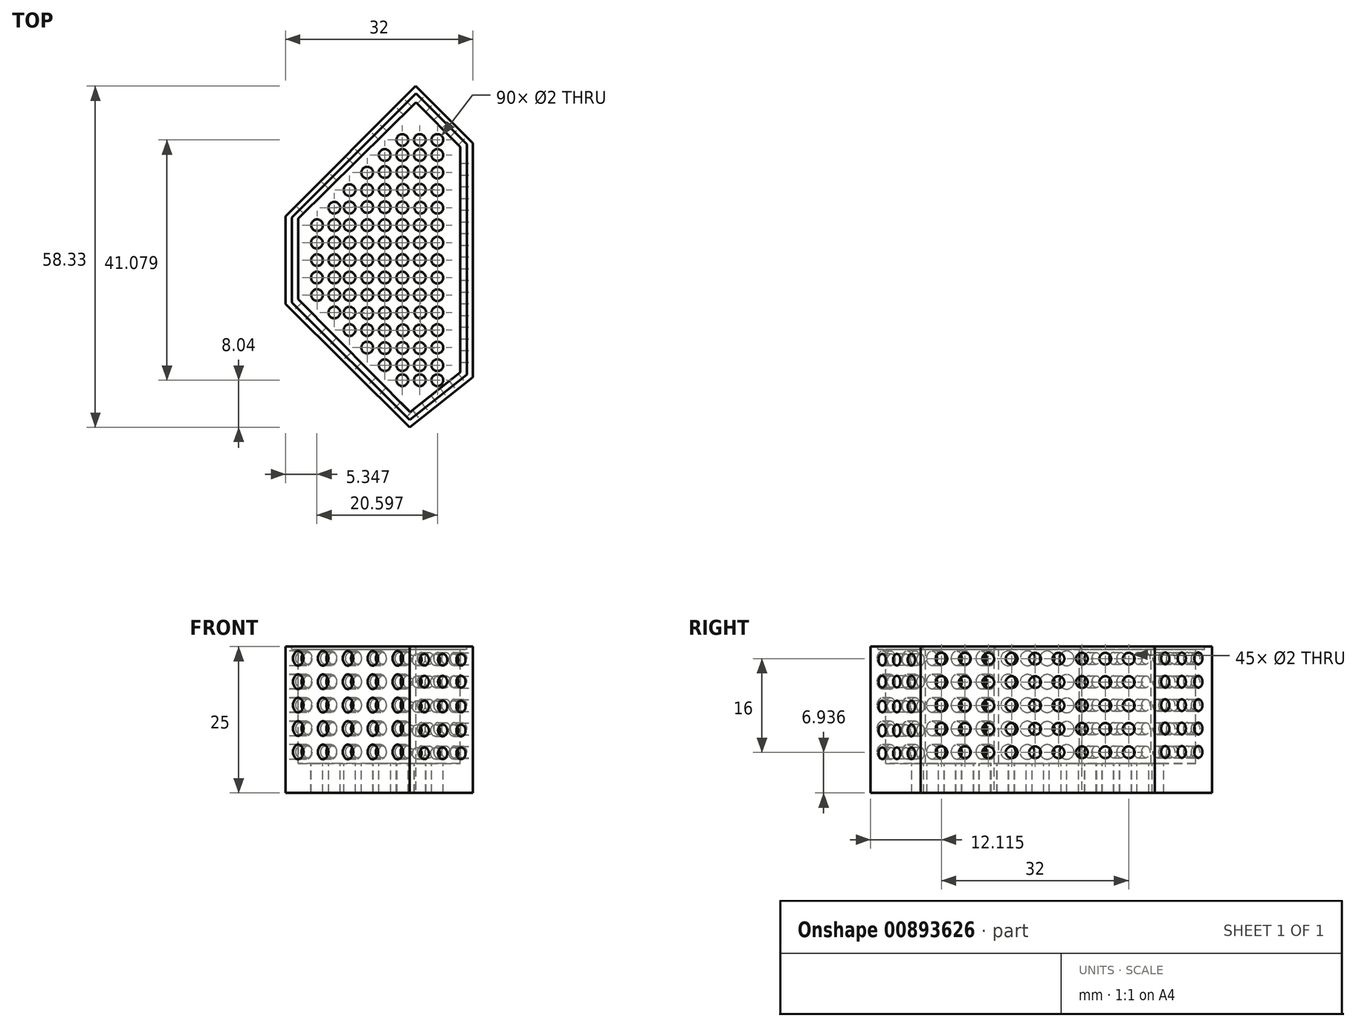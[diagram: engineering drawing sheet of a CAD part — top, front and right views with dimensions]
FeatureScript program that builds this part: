
annotation { "Feature Type Name" : "Feature", "Feature Type Description" : "" }
export const myFeature = defineFeature(function(context is Context, id is Id, definition is map)
    precondition{}
    {
        {
            var Q0;
            Q0=qCreatedBy(makeId("Top.planeOp"),FACE);
            var sketch = newSketch(context, id + "F0", { "sketchPlane" : qUnion([Q0])});
            skLineSegment(sketch, "E0", {"start": v(10.6, 0) * mm, "end": v(10.6, 7.5) * mm});
            skLineSegment(sketch, "E1", {"start": v(42.6, 0) * mm, "end": v(42.6, 20) * mm});
            skLineSegment(sketch, "E2", {"start": v(10.6, 7.5) * mm, "end": v(32.85, 29.75) * mm});
            skLineSegment(sketch, "E3", {"start": v(42.6, 20) * mm, "end": v(32.85, 29.75) * mm});
            skLineSegment(sketch, "E4", {"start": v(10.6, 0) * mm, "end": v(10.6, -7.5) * mm});
            skLineSegment(sketch, "E5", {"start": v(42.6, 0) * mm, "end": v(42.6, -20) * mm});
            skLineSegment(sketch, "E6", {"start": v(31.8, -28.58) * mm, "end": v(10.6, -7.5) * mm});
            skLineSegment(sketch, "E7", {"start": v(42.6, -20) * mm, "end": v(31.8, -28.58) * mm});
            skSolve(sketch);
        }
        {
            var Q0;
            Q0=makeQuery(id+"F0.imprint","IMPRINT",FACE,{"disambiguationData":[TD([[makeQuery(id+"F0.imprint","IMPRINT",EDGE,{"derivedFrom":sQuery(id+"F0.wireOp",EDGE,"E0")}),-1.0]])]});
            extrude(context, id + "F1", {"entities" : qUnion([Q0]), "depth" : 25 * mm, "offsetDistance" : 25 * mm});
        }
        {
            var Q0;
            Q0=makeQuery(id+"F1.opExtrude","CAP_FACE",FACE,{"disambiguationData":[OSD([sQuery(id+"F0.wireOp",EDGE,"E0"),sQuery(id+"F0.wireOp",EDGE,"E1"),sQuery(id+"F0.wireOp",EDGE,"E2"),sQuery(id+"F0.wireOp",EDGE,"E3"),sQuery(id+"F0.wireOp",EDGE,"E4"),sQuery(id+"F0.wireOp",EDGE,"E5"),sQuery(id+"F0.wireOp",EDGE,"E6"),sQuery(id+"F0.wireOp",EDGE,"E7")])],"isStart":false});
            var sketch = newSketch(context, id + "F2", { "sketchPlane" : qUnion([Q0])});
            skLineSegment(sketch, "E8", {"start": v(11.67, 0) * mm, "end": v(11.67, 7.32) * mm});
            skLineSegment(sketch, "E9", {"start": v(11.67, 7.32) * mm, "end": v(32.88, 28.52) * mm});
            skLineSegment(sketch, "E10", {"start": v(32.88, 28.52) * mm, "end": v(41.61, 19.79) * mm});
            skLineSegment(sketch, "E11", {"start": v(41.61, 19.79) * mm, "end": v(41.61, 0) * mm});
            skLineSegment(sketch, "E12", {"start": v(41.61, 0) * mm, "end": v(41.61, -19.55) * mm});
            skLineSegment(sketch, "E13", {"start": v(41.61, -19.55) * mm, "end": v(31.8, -27.35) * mm});
            skLineSegment(sketch, "E14", {"start": v(31.8, -27.35) * mm, "end": v(11.67, -7.23) * mm});
            skLineSegment(sketch, "E15", {"start": v(11.67, -7.23) * mm, "end": v(11.67, 0) * mm});
            skSolve(sketch);
        }
        {
            var Q0;
            Q0=makeQuery(id+"F2.imprint","IMPRINT",FACE,{"disambiguationData":[TD([[makeQuery(id+"F2.imprint","IMPRINT",EDGE,{"derivedFrom":sQuery(id+"F2.wireOp",EDGE,"E8")}),-1.0]])]});
            var sketch = newSketch(context, id + "F3", { "sketchPlane" : qUnion([Q0])});
            skLineSegment(sketch, "E16", {"start": v(12.76, 0) * mm, "end": v(12.76, 7.1) * mm});
            skLineSegment(sketch, "E17", {"start": v(12.76, 7.1) * mm, "end": v(32.86, 27) * mm});
            skLineSegment(sketch, "E18", {"start": v(32.86, 27) * mm, "end": v(40.43, 19.36) * mm});
            skLineSegment(sketch, "E19", {"start": v(40.43, 19.36) * mm, "end": v(40.43, 0) * mm});
            skLineSegment(sketch, "E20", {"start": v(40.43, 0) * mm, "end": v(40.43, -19.16) * mm});
            skLineSegment(sketch, "E21", {"start": v(40.43, -19.16) * mm, "end": v(31.9, -25.96) * mm});
            skLineSegment(sketch, "E22", {"start": v(31.9, -25.96) * mm, "end": v(12.76, -6.7) * mm});
            skLineSegment(sketch, "E23", {"start": v(12.76, -6.7) * mm, "end": v(12.76, 0) * mm});
            skSolve(sketch);
        }
        {
            var Q0;
            Q0=makeQuery(id+"F3.imprint","IMPRINT",FACE,{"disambiguationData":[TD([[makeQuery(id+"F3.imprint","IMPRINT",EDGE,{"derivedFrom":sQuery(id+"F3.wireOp",EDGE,"E16")}),-1.0]])]});
            extrude(context, id + "F4", {"entities" : qUnion([Q0]), "operationType" : NewBodyOperationType.REMOVE, "oppositeDirection" : true, "depth" : 20 * mm, "offsetDistance" : 25 * mm});
        }
        {
            var Q0;
            Q0=makeQuery(id+"F1.opExtrude","SWEPT_FACE",FACE,{"disambiguationData":[OSD([sQuery(id+"F0.wireOp",EDGE,"E1"),sQuery(id+"F0.wireOp",EDGE,"E5")])]});
            var sketch = newSketch(context, id + "F5", { "sketchPlane" : qUnion([Q0])});
            skLineSegment(sketch, "E24.bottom", {"start": v(-18.47, 22.94) * mm, "end": v(-16.47, 22.94) * mm});
            skLineSegment(sketch, "E24.top", {"start": v(-18.47, 20.94) * mm, "end": v(-16.47, 20.94) * mm});
            skLineSegment(sketch, "E24.left", {"start": v(-18.47, 22.94) * mm, "end": v(-18.47, 20.94) * mm});
            skLineSegment(sketch, "E24.right", {"start": v(-16.47, 22.94) * mm, "end": v(-16.47, 20.94) * mm});
            skPoint(sketch, "E25.oppositeSnap0", {"position": v(-14.47, 22.94) * mm});
            skLineSegment(sketch, "E25.bottom", {"start": v(-12.47, 22.94) * mm, "end": v(-14.47, 22.94) * mm});
            skLineSegment(sketch, "E25.top", {"start": v(-12.47, 20.94) * mm, "end": v(-14.47, 20.94) * mm});
            skLineSegment(sketch, "E25.left", {"start": v(-12.47, 22.94) * mm, "end": v(-12.47, 20.94) * mm});
            skLineSegment(sketch, "E25.right", {"start": v(-14.47, 22.94) * mm, "end": v(-14.47, 20.94) * mm});
            skLineSegment(sketch, "E26.bottom", {"start": v(-8.47, 22.94) * mm, "end": v(-10.47, 22.94) * mm});
            skLineSegment(sketch, "E26.top", {"start": v(-8.47, 20.94) * mm, "end": v(-10.47, 20.94) * mm});
            skLineSegment(sketch, "E26.left", {"start": v(-8.47, 22.94) * mm, "end": v(-8.47, 20.94) * mm});
            skLineSegment(sketch, "E26.right", {"start": v(-10.47, 22.94) * mm, "end": v(-10.47, 20.94) * mm});
            skLineSegment(sketch, "E27.bottom", {"start": v(-4.47, 22.94) * mm, "end": v(-6.47, 22.94) * mm});
            skLineSegment(sketch, "E27.top", {"start": v(-4.47, 20.94) * mm, "end": v(-6.47, 20.94) * mm});
            skLineSegment(sketch, "E27.left", {"start": v(-4.47, 22.94) * mm, "end": v(-4.47, 20.94) * mm});
            skLineSegment(sketch, "E27.right", {"start": v(-6.47, 22.94) * mm, "end": v(-6.47, 20.94) * mm});
            skPoint(sketch, "E28.oppositeSnap0", {"position": v(-2.47, 22.94) * mm});
            skLineSegment(sketch, "E28.bottom", {"start": v(-0.47, 22.94) * mm, "end": v(-2.47, 22.94) * mm});
            skLineSegment(sketch, "E28.top", {"start": v(-0.47, 20.94) * mm, "end": v(-2.47, 20.94) * mm});
            skLineSegment(sketch, "E28.left", {"start": v(-0.47, 22.94) * mm, "end": v(-0.47, 20.94) * mm});
            skLineSegment(sketch, "E28.right", {"start": v(-2.47, 22.94) * mm, "end": v(-2.47, 20.94) * mm});
            skLineSegment(sketch, "E29.bottom", {"start": v(3.53, 22.94) * mm, "end": v(1.53, 22.94) * mm});
            skLineSegment(sketch, "E29.top", {"start": v(3.53, 20.94) * mm, "end": v(1.53, 20.94) * mm});
            skLineSegment(sketch, "E29.left", {"start": v(3.53, 22.94) * mm, "end": v(3.53, 20.94) * mm});
            skLineSegment(sketch, "E29.right", {"start": v(1.53, 22.94) * mm, "end": v(1.53, 20.94) * mm});
            skLineSegment(sketch, "E30.bottom", {"start": v(7.53, 22.94) * mm, "end": v(5.53, 22.94) * mm});
            skLineSegment(sketch, "E30.top", {"start": v(7.53, 20.94) * mm, "end": v(5.53, 20.94) * mm});
            skLineSegment(sketch, "E30.left", {"start": v(7.53, 22.94) * mm, "end": v(7.53, 20.94) * mm});
            skLineSegment(sketch, "E30.right", {"start": v(5.53, 22.94) * mm, "end": v(5.53, 20.94) * mm});
            skLineSegment(sketch, "E31.bottom", {"start": v(11.53, 22.94) * mm, "end": v(9.53, 22.94) * mm});
            skLineSegment(sketch, "E31.top", {"start": v(11.53, 20.94) * mm, "end": v(9.53, 20.94) * mm});
            skLineSegment(sketch, "E31.left", {"start": v(11.53, 22.94) * mm, "end": v(11.53, 20.94) * mm});
            skLineSegment(sketch, "E31.right", {"start": v(9.53, 22.94) * mm, "end": v(9.53, 20.94) * mm});
            skLineSegment(sketch, "E32.bottom", {"start": v(15.53, 22.94) * mm, "end": v(13.53, 22.94) * mm});
            skLineSegment(sketch, "E32.top", {"start": v(15.53, 20.94) * mm, "end": v(13.53, 20.94) * mm});
            skLineSegment(sketch, "E32.left", {"start": v(15.53, 22.94) * mm, "end": v(15.53, 20.94) * mm});
            skLineSegment(sketch, "E32.right", {"start": v(13.53, 22.94) * mm, "end": v(13.53, 20.94) * mm});
            skLineSegment(sketch, "E33.bottom", {"start": v(-18.47, 16.94) * mm, "end": v(-16.47, 16.94) * mm});
            skLineSegment(sketch, "E33.top", {"start": v(-18.47, 18.94) * mm, "end": v(-16.47, 18.94) * mm});
            skLineSegment(sketch, "E33.left", {"start": v(-18.47, 16.94) * mm, "end": v(-18.47, 18.94) * mm});
            skLineSegment(sketch, "E33.right", {"start": v(-16.47, 16.94) * mm, "end": v(-16.47, 18.94) * mm});
            skLineSegment(sketch, "E34.bottom", {"start": v(-12.47, 16.94) * mm, "end": v(-14.47, 16.94) * mm});
            skLineSegment(sketch, "E34.top", {"start": v(-12.47, 18.94) * mm, "end": v(-14.47, 18.94) * mm});
            skLineSegment(sketch, "E34.left", {"start": v(-12.47, 16.94) * mm, "end": v(-12.47, 18.94) * mm});
            skLineSegment(sketch, "E34.right", {"start": v(-14.47, 16.94) * mm, "end": v(-14.47, 18.94) * mm});
            skLineSegment(sketch, "E35.bottom", {"start": v(-8.47, 16.94) * mm, "end": v(-10.47, 16.94) * mm});
            skLineSegment(sketch, "E35.top", {"start": v(-8.47, 18.94) * mm, "end": v(-10.47, 18.94) * mm});
            skLineSegment(sketch, "E35.left", {"start": v(-8.47, 16.94) * mm, "end": v(-8.47, 18.94) * mm});
            skLineSegment(sketch, "E35.right", {"start": v(-10.47, 16.94) * mm, "end": v(-10.47, 18.94) * mm});
            skLineSegment(sketch, "E36.bottom", {"start": v(-4.47, 16.94) * mm, "end": v(-6.47, 16.94) * mm});
            skLineSegment(sketch, "E36.top", {"start": v(-4.47, 18.94) * mm, "end": v(-6.47, 18.94) * mm});
            skLineSegment(sketch, "E36.left", {"start": v(-4.47, 16.94) * mm, "end": v(-4.47, 18.94) * mm});
            skLineSegment(sketch, "E36.right", {"start": v(-6.47, 16.94) * mm, "end": v(-6.47, 18.94) * mm});
            skLineSegment(sketch, "E37.bottom", {"start": v(-0.47, 16.94) * mm, "end": v(-2.47, 16.94) * mm});
            skLineSegment(sketch, "E37.top", {"start": v(-0.47, 18.94) * mm, "end": v(-2.47, 18.94) * mm});
            skLineSegment(sketch, "E37.left", {"start": v(-0.47, 16.94) * mm, "end": v(-0.47, 18.94) * mm});
            skLineSegment(sketch, "E37.right", {"start": v(-2.47, 16.94) * mm, "end": v(-2.47, 18.94) * mm});
            skLineSegment(sketch, "E38.bottom", {"start": v(3.53, 16.94) * mm, "end": v(1.53, 16.94) * mm});
            skLineSegment(sketch, "E38.top", {"start": v(3.53, 18.94) * mm, "end": v(1.53, 18.94) * mm});
            skLineSegment(sketch, "E38.left", {"start": v(3.53, 16.94) * mm, "end": v(3.53, 18.94) * mm});
            skLineSegment(sketch, "E38.right", {"start": v(1.53, 16.94) * mm, "end": v(1.53, 18.94) * mm});
            skLineSegment(sketch, "E39.bottom", {"start": v(7.53, 16.94) * mm, "end": v(5.53, 16.94) * mm});
            skLineSegment(sketch, "E39.top", {"start": v(7.53, 18.94) * mm, "end": v(5.53, 18.94) * mm});
            skLineSegment(sketch, "E39.left", {"start": v(7.53, 16.94) * mm, "end": v(7.53, 18.94) * mm});
            skLineSegment(sketch, "E39.right", {"start": v(5.53, 16.94) * mm, "end": v(5.53, 18.94) * mm});
            skLineSegment(sketch, "E40.bottom", {"start": v(11.53, 16.94) * mm, "end": v(9.53, 16.94) * mm});
            skLineSegment(sketch, "E40.top", {"start": v(11.53, 18.94) * mm, "end": v(9.53, 18.94) * mm});
            skLineSegment(sketch, "E40.left", {"start": v(11.53, 16.94) * mm, "end": v(11.53, 18.94) * mm});
            skLineSegment(sketch, "E40.right", {"start": v(9.53, 16.94) * mm, "end": v(9.53, 18.94) * mm});
            skLineSegment(sketch, "E41.bottom", {"start": v(15.53, 16.94) * mm, "end": v(13.53, 16.94) * mm});
            skLineSegment(sketch, "E41.top", {"start": v(15.53, 18.94) * mm, "end": v(13.53, 18.94) * mm});
            skLineSegment(sketch, "E41.left", {"start": v(15.53, 16.94) * mm, "end": v(15.53, 18.94) * mm});
            skLineSegment(sketch, "E41.right", {"start": v(13.53, 16.94) * mm, "end": v(13.53, 18.94) * mm});
            skLineSegment(sketch, "E42.bottom", {"start": v(-18.47, 12.94) * mm, "end": v(-16.47, 12.94) * mm});
            skLineSegment(sketch, "E42.top", {"start": v(-18.47, 14.94) * mm, "end": v(-16.47, 14.94) * mm});
            skLineSegment(sketch, "E42.left", {"start": v(-18.47, 12.94) * mm, "end": v(-18.47, 14.94) * mm});
            skLineSegment(sketch, "E42.right", {"start": v(-16.47, 12.94) * mm, "end": v(-16.47, 14.94) * mm});
            skLineSegment(sketch, "E43.bottom", {"start": v(-12.47, 12.94) * mm, "end": v(-14.47, 12.94) * mm});
            skLineSegment(sketch, "E43.top", {"start": v(-12.47, 14.94) * mm, "end": v(-14.47, 14.94) * mm});
            skLineSegment(sketch, "E43.left", {"start": v(-12.47, 12.94) * mm, "end": v(-12.47, 14.94) * mm});
            skLineSegment(sketch, "E43.right", {"start": v(-14.47, 12.94) * mm, "end": v(-14.47, 14.94) * mm});
            skLineSegment(sketch, "E44.bottom", {"start": v(-8.47, 12.94) * mm, "end": v(-10.47, 12.94) * mm});
            skLineSegment(sketch, "E44.top", {"start": v(-8.47, 14.94) * mm, "end": v(-10.47, 14.94) * mm});
            skLineSegment(sketch, "E44.left", {"start": v(-8.47, 12.94) * mm, "end": v(-8.47, 14.94) * mm});
            skLineSegment(sketch, "E44.right", {"start": v(-10.47, 12.94) * mm, "end": v(-10.47, 14.94) * mm});
            skLineSegment(sketch, "E45.bottom", {"start": v(-4.47, 12.94) * mm, "end": v(-6.47, 12.94) * mm});
            skLineSegment(sketch, "E45.top", {"start": v(-4.47, 14.94) * mm, "end": v(-6.47, 14.94) * mm});
            skLineSegment(sketch, "E45.left", {"start": v(-4.47, 12.94) * mm, "end": v(-4.47, 14.94) * mm});
            skLineSegment(sketch, "E45.right", {"start": v(-6.47, 12.94) * mm, "end": v(-6.47, 14.94) * mm});
            skLineSegment(sketch, "E46.bottom", {"start": v(-0.47, 12.94) * mm, "end": v(-2.47, 12.94) * mm});
            skLineSegment(sketch, "E46.top", {"start": v(-0.47, 14.94) * mm, "end": v(-2.47, 14.94) * mm});
            skLineSegment(sketch, "E46.left", {"start": v(-0.47, 12.94) * mm, "end": v(-0.47, 14.94) * mm});
            skLineSegment(sketch, "E46.right", {"start": v(-2.47, 12.94) * mm, "end": v(-2.47, 14.94) * mm});
            skLineSegment(sketch, "E47.bottom", {"start": v(3.53, 12.94) * mm, "end": v(3.53, 12.94) * mm});
            skLineSegment(sketch, "E47.top", {"start": v(3.53, 13.59) * mm, "end": v(3.53, 13.59) * mm});
            skLineSegment(sketch, "E47.left", {"start": v(3.53, 12.94) * mm, "end": v(3.53, 13.59) * mm});
            skLineSegment(sketch, "E47.right", {"start": v(3.53, 12.94) * mm, "end": v(3.53, 13.59) * mm});
            skLineSegment(sketch, "E48.bottom", {"start": v(3.53, 12.94) * mm, "end": v(1.53, 12.94) * mm});
            skLineSegment(sketch, "E48.top", {"start": v(3.53, 14.94) * mm, "end": v(1.53, 14.94) * mm});
            skLineSegment(sketch, "E48.left", {"start": v(3.53, 12.94) * mm, "end": v(3.53, 14.94) * mm});
            skLineSegment(sketch, "E48.right", {"start": v(1.53, 12.94) * mm, "end": v(1.53, 14.94) * mm});
            skLineSegment(sketch, "E49.bottom", {"start": v(7.53, 12.94) * mm, "end": v(5.53, 12.94) * mm});
            skLineSegment(sketch, "E49.top", {"start": v(7.53, 14.94) * mm, "end": v(5.53, 14.94) * mm});
            skLineSegment(sketch, "E49.left", {"start": v(7.53, 12.94) * mm, "end": v(7.53, 14.94) * mm});
            skLineSegment(sketch, "E49.right", {"start": v(5.53, 12.94) * mm, "end": v(5.53, 14.94) * mm});
            skLineSegment(sketch, "E50.bottom", {"start": v(11.53, 12.94) * mm, "end": v(9.53, 12.94) * mm});
            skLineSegment(sketch, "E50.top", {"start": v(11.53, 14.94) * mm, "end": v(9.53, 14.94) * mm});
            skLineSegment(sketch, "E50.left", {"start": v(11.53, 12.94) * mm, "end": v(11.53, 14.94) * mm});
            skLineSegment(sketch, "E50.right", {"start": v(9.53, 12.94) * mm, "end": v(9.53, 14.94) * mm});
            skLineSegment(sketch, "E51.bottom", {"start": v(15.53, 12.94) * mm, "end": v(13.53, 12.94) * mm});
            skLineSegment(sketch, "E51.top", {"start": v(15.53, 14.94) * mm, "end": v(13.53, 14.94) * mm});
            skLineSegment(sketch, "E51.left", {"start": v(15.53, 12.94) * mm, "end": v(15.53, 14.94) * mm});
            skLineSegment(sketch, "E51.right", {"start": v(13.53, 12.94) * mm, "end": v(13.53, 14.94) * mm});
            skLineSegment(sketch, "E52.MirrorCS", {"start": v(-18.47, 8.94) * mm, "end": v(-16.47, 8.94) * mm});
            skLineSegment(sketch, "E53.MirrorCS", {"start": v(-18.47, 10.94) * mm, "end": v(-18.47, 8.94) * mm});
            skLineSegment(sketch, "E54.top", {"start": v(-18.47, 10.94) * mm, "end": v(-16.47, 10.94) * mm});
            skLineSegment(sketch, "E54.left", {"start": v(-18.47, 8.94) * mm, "end": v(-18.47, 10.94) * mm});
            skLineSegment(sketch, "E54.right", {"start": v(-16.47, 8.94) * mm, "end": v(-16.47, 10.94) * mm});
            skLineSegment(sketch, "E55.bottom", {"start": v(-12.47, 8.94) * mm, "end": v(-14.47, 8.94) * mm});
            skLineSegment(sketch, "E55.top", {"start": v(-12.47, 10.94) * mm, "end": v(-14.47, 10.94) * mm});
            skLineSegment(sketch, "E55.left", {"start": v(-12.47, 8.94) * mm, "end": v(-12.47, 10.94) * mm});
            skLineSegment(sketch, "E55.right", {"start": v(-14.47, 8.94) * mm, "end": v(-14.47, 10.94) * mm});
            skLineSegment(sketch, "E56.bottom", {"start": v(-8.47, 8.94) * mm, "end": v(-10.47, 8.94) * mm});
            skLineSegment(sketch, "E56.top", {"start": v(-8.47, 10.94) * mm, "end": v(-10.47, 10.94) * mm});
            skLineSegment(sketch, "E56.left", {"start": v(-8.47, 8.94) * mm, "end": v(-8.47, 10.94) * mm});
            skLineSegment(sketch, "E56.right", {"start": v(-10.47, 8.94) * mm, "end": v(-10.47, 10.94) * mm});
            skLineSegment(sketch, "E57.bottom", {"start": v(-4.47, 8.94) * mm, "end": v(-6.47, 8.94) * mm});
            skLineSegment(sketch, "E57.top", {"start": v(-4.47, 10.94) * mm, "end": v(-6.47, 10.94) * mm});
            skLineSegment(sketch, "E57.left", {"start": v(-4.47, 8.94) * mm, "end": v(-4.47, 10.94) * mm});
            skLineSegment(sketch, "E57.right", {"start": v(-6.47, 8.94) * mm, "end": v(-6.47, 10.94) * mm});
            skLineSegment(sketch, "E58.bottom", {"start": v(-0.47, 8.94) * mm, "end": v(-2.47, 8.94) * mm});
            skLineSegment(sketch, "E58.top", {"start": v(-0.47, 10.94) * mm, "end": v(-2.47, 10.94) * mm});
            skLineSegment(sketch, "E58.left", {"start": v(-0.47, 8.94) * mm, "end": v(-0.47, 10.94) * mm});
            skLineSegment(sketch, "E58.right", {"start": v(-2.47, 8.94) * mm, "end": v(-2.47, 10.94) * mm});
            skLineSegment(sketch, "E59.bottom", {"start": v(3.53, 8.94) * mm, "end": v(1.53, 8.94) * mm});
            skLineSegment(sketch, "E59.top", {"start": v(3.53, 10.94) * mm, "end": v(1.53, 10.94) * mm});
            skLineSegment(sketch, "E59.left", {"start": v(3.53, 8.94) * mm, "end": v(3.53, 10.94) * mm});
            skLineSegment(sketch, "E59.right", {"start": v(1.53, 8.94) * mm, "end": v(1.53, 10.94) * mm});
            skLineSegment(sketch, "E60.bottom", {"start": v(7.53, 8.94) * mm, "end": v(5.53, 8.94) * mm});
            skLineSegment(sketch, "E60.top", {"start": v(7.53, 10.94) * mm, "end": v(5.53, 10.94) * mm});
            skLineSegment(sketch, "E60.left", {"start": v(7.53, 8.94) * mm, "end": v(7.53, 10.94) * mm});
            skLineSegment(sketch, "E60.right", {"start": v(5.53, 8.94) * mm, "end": v(5.53, 10.94) * mm});
            skLineSegment(sketch, "E61.bottom", {"start": v(11.53, 8.94) * mm, "end": v(9.53, 8.94) * mm});
            skLineSegment(sketch, "E61.top", {"start": v(11.53, 10.94) * mm, "end": v(9.53, 10.94) * mm});
            skLineSegment(sketch, "E61.left", {"start": v(11.53, 8.94) * mm, "end": v(11.53, 10.94) * mm});
            skLineSegment(sketch, "E61.right", {"start": v(9.53, 8.94) * mm, "end": v(9.53, 10.94) * mm});
            skLineSegment(sketch, "E62.bottom", {"start": v(15.53, 8.94) * mm, "end": v(13.53, 8.94) * mm});
            skLineSegment(sketch, "E62.top", {"start": v(15.53, 10.94) * mm, "end": v(13.53, 10.94) * mm});
            skLineSegment(sketch, "E62.left", {"start": v(15.53, 8.94) * mm, "end": v(15.53, 10.94) * mm});
            skLineSegment(sketch, "E62.right", {"start": v(13.53, 8.94) * mm, "end": v(13.53, 10.94) * mm});
            skLineSegment(sketch, "E63.bottom", {"start": v(-18.47, 4.94) * mm, "end": v(-16.47, 4.94) * mm});
            skLineSegment(sketch, "E63.top", {"start": v(-18.47, 6.94) * mm, "end": v(-16.47, 6.94) * mm});
            skLineSegment(sketch, "E63.left", {"start": v(-18.47, 4.94) * mm, "end": v(-18.47, 6.94) * mm});
            skLineSegment(sketch, "E63.right", {"start": v(-16.47, 4.94) * mm, "end": v(-16.47, 6.94) * mm});
            skLineSegment(sketch, "E64.bottom", {"start": v(-12.47, 4.94) * mm, "end": v(-14.47, 4.94) * mm});
            skLineSegment(sketch, "E64.top", {"start": v(-12.47, 6.96) * mm, "end": v(-14.47, 6.96) * mm});
            skLineSegment(sketch, "E64.left", {"start": v(-12.47, 4.94) * mm, "end": v(-12.47, 6.96) * mm});
            skLineSegment(sketch, "E64.right", {"start": v(-14.47, 4.94) * mm, "end": v(-14.47, 6.96) * mm});
            skLineSegment(sketch, "E65.bottom", {"start": v(-8.47, 4.94) * mm, "end": v(-10.47, 4.94) * mm});
            skLineSegment(sketch, "E65.top", {"start": v(-8.47, 6.94) * mm, "end": v(-10.47, 6.94) * mm});
            skLineSegment(sketch, "E65.left", {"start": v(-8.47, 4.94) * mm, "end": v(-8.47, 6.94) * mm});
            skLineSegment(sketch, "E65.right", {"start": v(-10.47, 4.94) * mm, "end": v(-10.47, 6.94) * mm});
            skLineSegment(sketch, "E66.bottom", {"start": v(-4.47, 4.94) * mm, "end": v(-6.47, 4.94) * mm});
            skLineSegment(sketch, "E66.top", {"start": v(-4.47, 6.94) * mm, "end": v(-6.47, 6.94) * mm});
            skLineSegment(sketch, "E66.left", {"start": v(-4.47, 4.94) * mm, "end": v(-4.47, 6.94) * mm});
            skLineSegment(sketch, "E66.right", {"start": v(-6.47, 4.94) * mm, "end": v(-6.47, 6.94) * mm});
            skLineSegment(sketch, "E67.bottom", {"start": v(-0.47, 4.94) * mm, "end": v(-2.47, 4.94) * mm});
            skLineSegment(sketch, "E67.top", {"start": v(-0.47, 6.94) * mm, "end": v(-2.47, 6.94) * mm});
            skLineSegment(sketch, "E67.left", {"start": v(-0.47, 4.94) * mm, "end": v(-0.47, 6.94) * mm});
            skLineSegment(sketch, "E67.right", {"start": v(-2.47, 4.94) * mm, "end": v(-2.47, 6.94) * mm});
            skLineSegment(sketch, "E68.bottom", {"start": v(3.53, 4.94) * mm, "end": v(1.53, 4.94) * mm});
            skLineSegment(sketch, "E68.top", {"start": v(3.53, 6.94) * mm, "end": v(1.53, 6.94) * mm});
            skLineSegment(sketch, "E68.left", {"start": v(3.53, 4.94) * mm, "end": v(3.53, 6.94) * mm});
            skLineSegment(sketch, "E68.right", {"start": v(1.53, 4.94) * mm, "end": v(1.53, 6.94) * mm});
            skLineSegment(sketch, "E69.bottom", {"start": v(7.53, 4.94) * mm, "end": v(5.53, 4.94) * mm});
            skLineSegment(sketch, "E69.top", {"start": v(7.53, 6.94) * mm, "end": v(5.53, 6.94) * mm});
            skLineSegment(sketch, "E69.left", {"start": v(7.53, 4.94) * mm, "end": v(7.53, 6.94) * mm});
            skLineSegment(sketch, "E69.right", {"start": v(5.53, 4.94) * mm, "end": v(5.53, 6.94) * mm});
            skLineSegment(sketch, "E70.bottom", {"start": v(11.53, 4.94) * mm, "end": v(9.53, 4.94) * mm});
            skLineSegment(sketch, "E70.top", {"start": v(11.53, 6.94) * mm, "end": v(9.53, 6.94) * mm});
            skLineSegment(sketch, "E70.left", {"start": v(11.53, 4.94) * mm, "end": v(11.53, 6.94) * mm});
            skLineSegment(sketch, "E70.right", {"start": v(9.53, 4.94) * mm, "end": v(9.53, 6.94) * mm});
            skLineSegment(sketch, "E71.bottom", {"start": v(15.53, 4.94) * mm, "end": v(13.53, 4.94) * mm});
            skLineSegment(sketch, "E71.top", {"start": v(15.53, 6.94) * mm, "end": v(13.53, 6.94) * mm});
            skLineSegment(sketch, "E71.left", {"start": v(15.53, 4.94) * mm, "end": v(15.53, 6.94) * mm});
            skLineSegment(sketch, "E71.right", {"start": v(13.53, 4.94) * mm, "end": v(13.53, 6.94) * mm});
            skSolve(sketch);
        }
        {
            var Q0;
            Q0=sQuery(id+"F5.wireOp",VERTEX,"E24.bottom.end");
            var Q1;
            Q1=sQuery(id+"F5.wireOp",VERTEX,"E25.bottom.start");
            var Q2;
            Q2=sQuery(id+"F5.wireOp",VERTEX,"E26.bottom.start");
            var Q3;
            Q3=sQuery(id+"F5.wireOp",VERTEX,"E27.bottom.start");
            var Q4;
            Q4=sQuery(id+"F5.wireOp",VERTEX,"E28.bottom.start");
            var Q5;
            Q5=sQuery(id+"F5.wireOp",VERTEX,"E29.bottom.start");
            var Q6;
            Q6=sQuery(id+"F5.wireOp",VERTEX,"E30.bottom.start");
            var Q7;
            Q7=sQuery(id+"F5.wireOp",VERTEX,"E31.bottom.start");
            var Q8;
            Q8=sQuery(id+"F5.wireOp",VERTEX,"E32.bottom.start");
            var Q9;
            Q9=sQuery(id+"F5.wireOp",VERTEX,"E33.top.end");
            var Q10;
            Q10=sQuery(id+"F5.wireOp",VERTEX,"E34.top.start");
            var Q11;
            Q11=sQuery(id+"F5.wireOp",VERTEX,"E35.top.start");
            var Q12;
            Q12=sQuery(id+"F5.wireOp",VERTEX,"E36.top.start");
            var Q13;
            Q13=sQuery(id+"F5.wireOp",VERTEX,"E37.top.start");
            var Q14;
            Q14=sQuery(id+"F5.wireOp",VERTEX,"E38.top.start");
            var Q15;
            Q15=sQuery(id+"F5.wireOp",VERTEX,"E39.top.start");
            var Q16;
            Q16=sQuery(id+"F5.wireOp",VERTEX,"E40.top.start");
            var Q17;
            Q17=sQuery(id+"F5.wireOp",VERTEX,"E41.top.start");
            var Q18;
            Q18=sQuery(id+"F5.wireOp",VERTEX,"E42.top.end");
            var Q19;
            Q19=sQuery(id+"F5.wireOp",VERTEX,"E43.top.start");
            var Q20;
            Q20=sQuery(id+"F5.wireOp",VERTEX,"E44.top.start");
            var Q21;
            Q21=sQuery(id+"F5.wireOp",VERTEX,"E46.top.start");
            var Q22;
            Q22=sQuery(id+"F5.wireOp",VERTEX,"E48.top.start");
            var Q23;
            Q23=sQuery(id+"F5.wireOp",VERTEX,"E49.top.start");
            var Q24;
            Q24=sQuery(id+"F5.wireOp",VERTEX,"E50.top.start");
            var Q25;
            Q25=sQuery(id+"F5.wireOp",VERTEX,"E45.top.start");
            var Q26;
            Q26=sQuery(id+"F5.wireOp",VERTEX,"E51.top.start");
            var Q27;
            Q27=sQuery(id+"F5.wireOp",VERTEX,"E54.top.end");
            var Q28;
            Q28=sQuery(id+"F5.wireOp",VERTEX,"E55.top.start");
            var Q29;
            Q29=sQuery(id+"F5.wireOp",VERTEX,"E56.top.start");
            var Q30;
            Q30=sQuery(id+"F5.wireOp",VERTEX,"E57.top.start");
            var Q31;
            Q31=sQuery(id+"F5.wireOp",VERTEX,"E58.top.start");
            var Q32;
            Q32=sQuery(id+"F5.wireOp",VERTEX,"E59.top.start");
            var Q33;
            Q33=sQuery(id+"F5.wireOp",VERTEX,"E60.top.start");
            var Q34;
            Q34=sQuery(id+"F5.wireOp",VERTEX,"E62.top.start");
            var Q35;
            Q35=sQuery(id+"F5.wireOp",VERTEX,"E61.top.start");
            var Q36;
            Q36=sQuery(id+"F5.wireOp",VERTEX,"E63.top.end");
            var Q37;
            Q37=sQuery(id+"F5.wireOp",VERTEX,"E64.top.start");
            var Q38;
            Q38=sQuery(id+"F5.wireOp",VERTEX,"E65.top.start");
            var Q39;
            Q39=sQuery(id+"F5.wireOp",VERTEX,"E66.top.start");
            var Q40;
            Q40=sQuery(id+"F5.wireOp",VERTEX,"E67.top.start");
            var Q41;
            Q41=sQuery(id+"F5.wireOp",VERTEX,"E68.top.start");
            var Q42;
            Q42=sQuery(id+"F5.wireOp",VERTEX,"E70.top.start");
            var Q43;
            Q43=sQuery(id+"F5.wireOp",VERTEX,"E69.top.start");
            var Q44;
            Q44=sQuery(id+"F5.wireOp",VERTEX,"E71.top.start");
            var Q45;
            Q45=makeQuery(id+"F1.opExtrude","SWEPT_BODY",BODY,{"disambiguationData":[OSD([sQuery(id+"F0.wireOp",EDGE,"E0"),sQuery(id+"F0.wireOp",EDGE,"E1"),sQuery(id+"F0.wireOp",EDGE,"E2"),sQuery(id+"F0.wireOp",EDGE,"E3"),sQuery(id+"F0.wireOp",EDGE,"E4"),sQuery(id+"F0.wireOp",EDGE,"E5"),sQuery(id+"F0.wireOp",EDGE,"E6"),sQuery(id+"F0.wireOp",EDGE,"E7")])]});
            hole(context, id + "F6", {"style" : HoleStyle.SIMPLE, "endStyle" : HoleEndStyle.BLIND, "holeDiameter" : 2 * mm, "majorDiameter" : 5 * mm, "holeDepth" : 12 * mm, "isTappedThrough" : true, "tappedDepth" : 12 * mm, "tapClearance" : 3, "startFromSketch" : true, "locations" : qUnion([Q0, Q1, Q2, Q3, Q4, Q5, Q6, Q7, Q8, Q9, Q10, Q11, Q12, Q13, Q14, Q15, Q16, Q17, Q18, Q19, Q20, Q21, Q22, Q23, Q24, Q25, Q26, Q27, Q28, Q29, Q30, Q31, Q32, Q33, Q34, Q35, Q36, Q37, Q38, Q39, Q40, Q41, Q42, Q43, Q44]), "scope" : qUnion([Q45])});
        }
        {
            var Q0;
            Q0=makeQuery(id+"F1.opExtrude","SWEPT_FACE",FACE,{"disambiguationData":[OSD([sQuery(id+"F0.wireOp",EDGE,"E7")])]});
            var sketch = newSketch(context, id + "F7", { "sketchPlane" : qUnion([Q0])});
            skLineSegment(sketch, "E72.bottom", {"start": v(18.3, 22.76) * mm, "end": v(10.3, 22.76) * mm});
            skLineSegment(sketch, "E72.top", {"start": v(18.3, 6.76) * mm, "end": v(10.3, 6.76) * mm});
            skLineSegment(sketch, "E72.left", {"start": v(18.3, 22.76) * mm, "end": v(18.3, 6.76) * mm});
            skLineSegment(sketch, "E72.right", {"start": v(10.3, 22.76) * mm, "end": v(10.3, 6.76) * mm});
            skLineSegment(sketch, "E73", {"start": v(14.3, 22.76) * mm, "end": v(14.3, 6.76) * mm});
            skLineSegment(sketch, "E74", {"start": v(10.3, 14.76) * mm, "end": v(18.3, 14.76) * mm});
            skLineSegment(sketch, "E75", {"start": v(10.3, 19) * mm, "end": v(18.3, 19) * mm});
            skLineSegment(sketch, "E76", {"start": v(18.3, 10.67) * mm, "end": v(10.3, 10.67) * mm});
            skLineSegment(sketch, "E77", {"start": v(14.3, 19) * mm, "end": v(10.3, 14.76) * mm});
            skLineSegment(sketch, "E78", {"start": v(14.3, 10.67) * mm, "end": v(10.3, 14.76) * mm});
            skLineSegment(sketch, "E79", {"start": v(14.3, 14.76) * mm, "end": v(18.3, 19) * mm});
            skSolve(sketch);
        }
        {
            var Q0;
            Q0=sQuery(id+"F7.wireOp",VERTEX,"E72.bottom.end");
            var Q1;
            Q1=sQuery(id+"F7.wireOp",VERTEX,"E73.start");
            var Q2;
            Q2=sQuery(id+"F7.wireOp",VERTEX,"E72.bottom.start");
            var Q3;
            Q3=sQuery(id+"F7.wireOp",VERTEX,"E75.end");
            var Q4;
            Q4=sQuery(id+"F7.wireOp",VERTEX,"E77.start");
            var Q5;
            Q5=sQuery(id+"F7.wireOp",VERTEX,"E75.start");
            var Q6;
            Q6=sQuery(id+"F7.wireOp",VERTEX,"E74.start");
            var Q7;
            Q7=sQuery(id+"F7.wireOp",VERTEX,"E79.start");
            var Q8;
            Q8=sQuery(id+"F7.wireOp",VERTEX,"E74.end");
            var Q9;
            Q9=sQuery(id+"F7.wireOp",VERTEX,"E76.end");
            var Q10;
            Q10=sQuery(id+"F7.wireOp",VERTEX,"E78.start");
            var Q11;
            Q11=sQuery(id+"F7.wireOp",VERTEX,"E76.start");
            var Q12;
            Q12=sQuery(id+"F7.wireOp",VERTEX,"E73.end");
            var Q13;
            Q13=sQuery(id+"F7.wireOp",VERTEX,"E72.top.start");
            var Q14;
            Q14=sQuery(id+"F7.wireOp",VERTEX,"E72.top.end");
            var Q15;
            Q15=makeQuery(id+"F1.opExtrude","SWEPT_BODY",BODY,{"disambiguationData":[OSD([sQuery(id+"F0.wireOp",EDGE,"E0"),sQuery(id+"F0.wireOp",EDGE,"E1"),sQuery(id+"F0.wireOp",EDGE,"E2"),sQuery(id+"F0.wireOp",EDGE,"E3"),sQuery(id+"F0.wireOp",EDGE,"E4"),sQuery(id+"F0.wireOp",EDGE,"E5"),sQuery(id+"F0.wireOp",EDGE,"E6"),sQuery(id+"F0.wireOp",EDGE,"E7")])]});
            hole(context, id + "F8", {"style" : HoleStyle.SIMPLE, "endStyle" : HoleEndStyle.BLIND, "holeDiameter" : 2 * mm, "majorDiameter" : 5 * mm, "holeDepth" : 4 * mm, "isTappedThrough" : true, "tappedDepth" : 12 * mm, "tapClearance" : 3, "startFromSketch" : true, "locations" : qUnion([Q0, Q1, Q2, Q3, Q4, Q5, Q6, Q7, Q8, Q9, Q10, Q11, Q12, Q13, Q14]), "scope" : qUnion([Q15])});
        }
        {
            var Q0;
            Q0=makeQuery(id+"F1.opExtrude","SWEPT_FACE",FACE,{"disambiguationData":[OSD([sQuery(id+"F0.wireOp",EDGE,"E3")])]});
            var sketch = newSketch(context, id + "F9", { "sketchPlane" : qUnion([Q0])});
            skLineSegment(sketch, "E80.bottom", {"start": v(-13.48, 23) * mm, "end": v(-5.48, 23) * mm});
            skLineSegment(sketch, "E80.top", {"start": v(-13.48, 7) * mm, "end": v(-5.48, 7) * mm});
            skLineSegment(sketch, "E80.left", {"start": v(-13.48, 23) * mm, "end": v(-13.48, 7) * mm});
            skLineSegment(sketch, "E80.right", {"start": v(-5.48, 23) * mm, "end": v(-5.48, 7) * mm});
            skLineSegment(sketch, "E81", {"start": v(-5.48, 15) * mm, "end": v(-5.48, 19) * mm});
            skLineSegment(sketch, "E82", {"start": v(-5.48, 15) * mm, "end": v(-13.48, 15) * mm});
            skLineSegment(sketch, "E83", {"start": v(-13.48, 19) * mm, "end": v(-5.48, 19) * mm});
            skLineSegment(sketch, "E84", {"start": v(-13.48, 11) * mm, "end": v(-5.48, 11) * mm});
            skLineSegment(sketch, "E85", {"start": v(-9.48, 23) * mm, "end": v(-9.48, 7) * mm});
            skLineSegment(sketch, "E86", {"start": v(-13.48, 23) * mm, "end": v(-9.48, 19) * mm});
            skLineSegment(sketch, "E87", {"start": v(-9.48, 15) * mm, "end": v(-13.48, 19) * mm});
            skLineSegment(sketch, "E88", {"start": v(-9.48, 11) * mm, "end": v(-13.48, 15) * mm});
            skSolve(sketch);
        }
        {
            var Q0;
            Q0=sQuery(id+"F9.wireOp",VERTEX,"E80.bottom.start");
            var Q1;
            Q1=sQuery(id+"F9.wireOp",VERTEX,"E85.start");
            var Q2;
            Q2=sQuery(id+"F9.wireOp",VERTEX,"E80.bottom.end");
            var Q3;
            Q3=sQuery(id+"F9.wireOp",VERTEX,"E86.end");
            var Q4;
            Q4=sQuery(id+"F9.wireOp",VERTEX,"E81.end");
            var Q5;
            Q5=sQuery(id+"F9.wireOp",VERTEX,"E83.start");
            var Q6;
            Q6=sQuery(id+"F9.wireOp",VERTEX,"E82.end");
            var Q7;
            Q7=sQuery(id+"F9.wireOp",VERTEX,"E87.start");
            var Q8;
            Q8=sQuery(id+"F9.wireOp",VERTEX,"E81.start");
            var Q9;
            Q9=sQuery(id+"F9.wireOp",VERTEX,"E84.start");
            var Q10;
            Q10=sQuery(id+"F9.wireOp",VERTEX,"E88.start");
            var Q11;
            Q11=sQuery(id+"F9.wireOp",VERTEX,"E84.end");
            var Q12;
            Q12=sQuery(id+"F9.wireOp",VERTEX,"E80.top.start");
            var Q13;
            Q13=sQuery(id+"F9.wireOp",VERTEX,"E80.top.end");
            var Q14;
            Q14=sQuery(id+"F9.wireOp",VERTEX,"E85.end");
            var Q15;
            Q15=makeQuery(id+"F1.opExtrude","SWEPT_BODY",BODY,{"disambiguationData":[OSD([sQuery(id+"F0.wireOp",EDGE,"E0"),sQuery(id+"F0.wireOp",EDGE,"E1"),sQuery(id+"F0.wireOp",EDGE,"E2"),sQuery(id+"F0.wireOp",EDGE,"E3"),sQuery(id+"F0.wireOp",EDGE,"E4"),sQuery(id+"F0.wireOp",EDGE,"E5"),sQuery(id+"F0.wireOp",EDGE,"E6"),sQuery(id+"F0.wireOp",EDGE,"E7")])]});
            hole(context, id + "F10", {"style" : HoleStyle.SIMPLE, "endStyle" : HoleEndStyle.BLIND, "holeDiameter" : 2 * mm, "majorDiameter" : 5 * mm, "holeDepth" : 4 * mm, "isTappedThrough" : true, "tappedDepth" : 12 * mm, "tapClearance" : 3, "startFromSketch" : true, "locations" : qUnion([Q0, Q1, Q2, Q3, Q4, Q5, Q6, Q7, Q8, Q9, Q10, Q11, Q12, Q13, Q14]), "scope" : qUnion([Q15])});
        }
        {
            var Q0;
            Q0=makeQuery(id+"F1.opExtrude","SWEPT_FACE",FACE,{"disambiguationData":[OSD([sQuery(id+"F0.wireOp",EDGE,"E6")])]});
            var sketch = newSketch(context, id + "F11", { "sketchPlane" : qUnion([Q0])});
            skLineSegment(sketch, "E89.bottom", {"start": v(15.84, 23) * mm, "end": v(39.84, 23) * mm});
            skLineSegment(sketch, "E89.top", {"start": v(15.84, 7) * mm, "end": v(39.84, 7) * mm});
            skLineSegment(sketch, "E89.left", {"start": v(15.84, 23) * mm, "end": v(15.84, 7) * mm});
            skLineSegment(sketch, "E89.right", {"start": v(39.84, 23) * mm, "end": v(39.84, 7) * mm});
            skLineSegment(sketch, "E90", {"start": v(27.84, 23) * mm, "end": v(27.84, 7) * mm});
            skLineSegment(sketch, "E91", {"start": v(39.84, 15) * mm, "end": v(15.84, 15) * mm});
            skLineSegment(sketch, "E92", {"start": v(15.84, 15) * mm, "end": v(39.84, 23) * mm});
            skLineSegment(sketch, "E93", {"start": v(15.84, 7) * mm, "end": v(39.84, 15) * mm});
            skLineSegment(sketch, "E94", {"start": v(27.84, 19) * mm, "end": v(39.84, 19) * mm});
            skLineSegment(sketch, "E95", {"start": v(27.84, 11) * mm, "end": v(39.84, 11) * mm});
            skLineSegment(sketch, "E96", {"start": v(27.84, 19) * mm, "end": v(15.84, 19) * mm});
            skLineSegment(sketch, "E97", {"start": v(27.84, 11) * mm, "end": v(15.84, 11) * mm});
            skLineSegment(sketch, "E98", {"start": v(27.84, 23) * mm, "end": v(39.84, 7) * mm});
            skLineSegment(sketch, "E99", {"start": v(39.84, 23) * mm, "end": v(27.84, 7) * mm});
            skLineSegment(sketch, "E100", {"start": v(33.84, 15) * mm, "end": v(33.84, 23) * mm});
            skLineSegment(sketch, "E101", {"start": v(33.84, 23) * mm, "end": v(33.84, 15) * mm});
            skLineSegment(sketch, "E102", {"start": v(33.84, 15) * mm, "end": v(33.84, 7) * mm});
            skLineSegment(sketch, "E103", {"start": v(15.84, 23) * mm, "end": v(27.84, 7) * mm});
            skLineSegment(sketch, "E104", {"start": v(27.84, 23) * mm, "end": v(15.84, 7) * mm});
            skLineSegment(sketch, "E105", {"start": v(21.84, 15) * mm, "end": v(21.84, 23) * mm});
            skLineSegment(sketch, "E106", {"start": v(21.84, 15) * mm, "end": v(21.84, 7) * mm});
            skLineSegment(sketch, "E107", {"start": v(21.84, 19) * mm, "end": v(15.84, 15) * mm});
            skLineSegment(sketch, "E108", {"start": v(21.84, 11) * mm, "end": v(27.84, 15) * mm});
            skLineSegment(sketch, "E109", {"start": v(27.84, 15) * mm, "end": v(33.84, 11) * mm});
            skLineSegment(sketch, "E110", {"start": v(33.84, 11) * mm, "end": v(33.84, 19) * mm});
            skLineSegment(sketch, "E111", {"start": v(33.84, 19) * mm, "end": v(27.84, 15) * mm});
            skSolve(sketch);
        }
        {
            var Q0;
            Q0=sQuery(id+"F11.wireOp",VERTEX,"E89.bottom.start");
            var Q1;
            Q1=sQuery(id+"F11.wireOp",VERTEX,"E105.end");
            var Q2;
            Q2=sQuery(id+"F11.wireOp",VERTEX,"E90.start");
            var Q3;
            Q3=sQuery(id+"F11.wireOp",VERTEX,"E100.end");
            var Q4;
            Q4=sQuery(id+"F11.wireOp",VERTEX,"E89.bottom.end");
            var Q5;
            Q5=sQuery(id+"F11.wireOp",VERTEX,"E96.end");
            var Q6;
            Q6=sQuery(id+"F11.wireOp",VERTEX,"E107.start");
            var Q7;
            Q7=sQuery(id+"F11.wireOp",VERTEX,"E94.start");
            var Q8;
            Q8=sQuery(id+"F11.wireOp",VERTEX,"E110.end");
            var Q9;
            Q9=sQuery(id+"F11.wireOp",VERTEX,"E94.end");
            var Q10;
            Q10=sQuery(id+"F11.wireOp",VERTEX,"E91.end");
            var Q11;
            Q11=sQuery(id+"F11.wireOp",VERTEX,"E105.start");
            var Q12;
            Q12=sQuery(id+"F11.wireOp",VERTEX,"E108.end");
            var Q13;
            Q13=sQuery(id+"F11.wireOp",VERTEX,"E100.start");
            var Q14;
            Q14=sQuery(id+"F11.wireOp",VERTEX,"E91.start");
            var Q15;
            Q15=sQuery(id+"F11.wireOp",VERTEX,"E97.end");
            var Q16;
            Q16=sQuery(id+"F11.wireOp",VERTEX,"E108.start");
            var Q17;
            Q17=sQuery(id+"F11.wireOp",VERTEX,"E95.start");
            var Q18;
            Q18=sQuery(id+"F11.wireOp",VERTEX,"E109.end");
            var Q19;
            Q19=sQuery(id+"F11.wireOp",VERTEX,"E95.end");
            var Q20;
            Q20=sQuery(id+"F11.wireOp",VERTEX,"E89.top.start");
            var Q21;
            Q21=sQuery(id+"F11.wireOp",VERTEX,"E106.end");
            var Q22;
            Q22=sQuery(id+"F11.wireOp",VERTEX,"E90.end");
            var Q23;
            Q23=sQuery(id+"F11.wireOp",VERTEX,"E102.end");
            var Q24;
            Q24=sQuery(id+"F11.wireOp",VERTEX,"E89.top.end");
            var Q25;
            Q25=makeQuery(id+"F1.opExtrude","SWEPT_BODY",BODY,{"disambiguationData":[OSD([sQuery(id+"F0.wireOp",EDGE,"E0"),sQuery(id+"F0.wireOp",EDGE,"E1"),sQuery(id+"F0.wireOp",EDGE,"E2"),sQuery(id+"F0.wireOp",EDGE,"E3"),sQuery(id+"F0.wireOp",EDGE,"E4"),sQuery(id+"F0.wireOp",EDGE,"E5"),sQuery(id+"F0.wireOp",EDGE,"E6"),sQuery(id+"F0.wireOp",EDGE,"E7")])]});
            hole(context, id + "F12", {"style" : HoleStyle.SIMPLE, "endStyle" : HoleEndStyle.BLIND, "holeDiameter" : 2.5 * mm, "majorDiameter" : 5 * mm, "holeDepth" : 4 * mm, "isTappedThrough" : true, "tappedDepth" : 12 * mm, "tapClearance" : 3, "startFromSketch" : true, "locations" : qUnion([Q0, Q1, Q2, Q3, Q4, Q5, Q6, Q7, Q8, Q9, Q10, Q11, Q12, Q13, Q14, Q15, Q16, Q17, Q18, Q19, Q20, Q21, Q22, Q23, Q24]), "scope" : qUnion([Q25])});
        }
        {
            var Q0;
            Q0=makeQuery(id+"F1.opExtrude","SWEPT_FACE",FACE,{"disambiguationData":[OSD([sQuery(id+"F0.wireOp",EDGE,"E2")])]});
            var sketch = newSketch(context, id + "F13", { "sketchPlane" : qUnion([Q0])});
            skLineSegment(sketch, "E112.bottom", {"start": v(-40.3, 23) * mm, "end": v(-16.3, 23) * mm});
            skLineSegment(sketch, "E112.top", {"start": v(-40.3, 7) * mm, "end": v(-16.3, 7) * mm});
            skLineSegment(sketch, "E112.left", {"start": v(-40.3, 23) * mm, "end": v(-40.3, 7) * mm});
            skLineSegment(sketch, "E112.right", {"start": v(-16.3, 23) * mm, "end": v(-16.3, 7) * mm});
            skLineSegment(sketch, "E113", {"start": v(-28.3, 23) * mm, "end": v(-28.3, 7) * mm});
            skLineSegment(sketch, "E114", {"start": v(-16.3, 15) * mm, "end": v(-40.3, 15) * mm});
            skLineSegment(sketch, "E115", {"start": v(-40.3, 7) * mm, "end": v(-16.3, 23) * mm});
            skLineSegment(sketch, "E116", {"start": v(-40.3, 23) * mm, "end": v(-16.3, 7) * mm});
            skLineSegment(sketch, "E117", {"start": v(-16.3, 19) * mm, "end": v(-40.3, 19) * mm});
            skLineSegment(sketch, "E118", {"start": v(-40.3, 11) * mm, "end": v(-16.3, 11) * mm});
            skLineSegment(sketch, "E119", {"start": v(-34.3, 19) * mm, "end": v(-34.3, 7) * mm});
            skLineSegment(sketch, "E120", {"start": v(-22.3, 19) * mm, "end": v(-22.3, 7) * mm});
            skLineSegment(sketch, "E121", {"start": v(-22.3, 19) * mm, "end": v(-22.3, 23) * mm});
            skLineSegment(sketch, "E122", {"start": v(-34.3, 19) * mm, "end": v(-34.3, 23) * mm});
            skLineSegment(sketch, "E123", {"start": v(-34.3, 15) * mm, "end": v(-40.3, 11) * mm});
            skLineSegment(sketch, "E124", {"start": v(-22.3, 15) * mm, "end": v(-16.3, 11) * mm});
            skLineSegment(sketch, "E125", {"start": v(-28.3, 11) * mm, "end": v(-34.3, 7) * mm});
            skLineSegment(sketch, "E126", {"start": v(-28.3, 19) * mm, "end": v(-22.3, 23) * mm});
            skLineSegment(sketch, "E127", {"start": v(-22.3, 11) * mm, "end": v(-28.3, 7) * mm});
            skLineSegment(sketch, "E128", {"start": v(-28.3, 15) * mm, "end": v(-40.3, 19) * mm});
            skLineSegment(sketch, "E129", {"start": v(-40.3, 15) * mm, "end": v(-34.3, 11) * mm});
            skSolve(sketch);
        }
        {
            var Q0;
            Q0=sQuery(id+"F13.wireOp",VERTEX,"E112.bottom.start");
            var Q1;
            Q1=sQuery(id+"F13.wireOp",VERTEX,"E122.end");
            var Q2;
            Q2=sQuery(id+"F13.wireOp",VERTEX,"E113.start");
            var Q3;
            Q3=sQuery(id+"F13.wireOp",VERTEX,"E121.end");
            var Q4;
            Q4=sQuery(id+"F13.wireOp",VERTEX,"E112.bottom.end");
            var Q5;
            Q5=sQuery(id+"F13.wireOp",VERTEX,"E117.end");
            var Q6;
            Q6=sQuery(id+"F13.wireOp",VERTEX,"E119.start");
            var Q7;
            Q7=sQuery(id+"F13.wireOp",VERTEX,"E126.start");
            var Q8;
            Q8=sQuery(id+"F13.wireOp",VERTEX,"E120.start");
            var Q9;
            Q9=sQuery(id+"F13.wireOp",VERTEX,"E117.start");
            var Q10;
            Q10=sQuery(id+"F13.wireOp",VERTEX,"E114.end");
            var Q11;
            Q11=sQuery(id+"F13.wireOp",VERTEX,"E128.start");
            var Q12;
            Q12=sQuery(id+"F13.wireOp",VERTEX,"E123.start");
            var Q13;
            Q13=sQuery(id+"F13.wireOp",VERTEX,"E124.start");
            var Q14;
            Q14=sQuery(id+"F13.wireOp",VERTEX,"E118.start");
            var Q15;
            Q15=sQuery(id+"F13.wireOp",VERTEX,"E129.end");
            var Q16;
            Q16=sQuery(id+"F13.wireOp",VERTEX,"E125.start");
            var Q17;
            Q17=sQuery(id+"F13.wireOp",VERTEX,"E114.start");
            var Q18;
            Q18=sQuery(id+"F13.wireOp",VERTEX,"E127.start");
            var Q19;
            Q19=sQuery(id+"F13.wireOp",VERTEX,"E118.end");
            var Q20;
            Q20=sQuery(id+"F13.wireOp",VERTEX,"E112.top.start");
            var Q21;
            Q21=sQuery(id+"F13.wireOp",VERTEX,"E113.end");
            var Q22;
            Q22=sQuery(id+"F13.wireOp",VERTEX,"E119.end");
            var Q23;
            Q23=sQuery(id+"F13.wireOp",VERTEX,"E120.end");
            var Q24;
            Q24=sQuery(id+"F13.wireOp",VERTEX,"E112.top.end");
            var Q25;
            Q25=makeQuery(id+"F1.opExtrude","SWEPT_BODY",BODY,{"disambiguationData":[OSD([sQuery(id+"F0.wireOp",EDGE,"E0"),sQuery(id+"F0.wireOp",EDGE,"E1"),sQuery(id+"F0.wireOp",EDGE,"E2"),sQuery(id+"F0.wireOp",EDGE,"E3"),sQuery(id+"F0.wireOp",EDGE,"E4"),sQuery(id+"F0.wireOp",EDGE,"E5"),sQuery(id+"F0.wireOp",EDGE,"E6"),sQuery(id+"F0.wireOp",EDGE,"E7")])]});
            hole(context, id + "F14", {"style" : HoleStyle.SIMPLE, "endStyle" : HoleEndStyle.BLIND, "holeDiameter" : 2 * mm, "majorDiameter" : 5 * mm, "holeDepth" : 4 * mm, "isTappedThrough" : true, "tappedDepth" : 12 * mm, "tapClearance" : 3, "startFromSketch" : true, "locations" : qUnion([Q0, Q1, Q2, Q3, Q4, Q5, Q6, Q7, Q8, Q9, Q10, Q11, Q12, Q13, Q14, Q15, Q16, Q17, Q18, Q19, Q20, Q21, Q22, Q23, Q24]), "scope" : qUnion([Q25])});
        }
        {
            var Q0;
            Q0=makeQuery(id+"F1.opExtrude","SWEPT_FACE",FACE,{"disambiguationData":[OSD([sQuery(id+"F0.wireOp",EDGE,"E0"),sQuery(id+"F0.wireOp",EDGE,"E4")])]});
            var sketch = newSketch(context, id + "F15", { "sketchPlane" : qUnion([Q0])});
            skLineSegment(sketch, "E130.bottom", {"start": v(-4.93, 23) * mm, "end": v(5.07, 23) * mm});
            skLineSegment(sketch, "E130.top", {"start": v(-4.93, 7) * mm, "end": v(5.07, 7) * mm});
            skLineSegment(sketch, "E130.left", {"start": v(-4.93, 23) * mm, "end": v(-4.93, 7) * mm});
            skLineSegment(sketch, "E130.right", {"start": v(5.07, 23) * mm, "end": v(5.07, 7) * mm});
            skLineSegment(sketch, "E131", {"start": v(1.78, 15) * mm, "end": v(-2.42, 14.98) * mm});
            skLineSegment(sketch, "E132", {"start": v(1.78, 15) * mm, "end": v(1.74, 23) * mm});
            skLineSegment(sketch, "E133", {"start": v(1.78, 15) * mm, "end": v(5.07, 15.01) * mm});
            skLineSegment(sketch, "E134", {"start": v(-2.42, 14.98) * mm, "end": v(-4.93, 14.97) * mm});
            skLineSegment(sketch, "E135", {"start": v(0.07, 19) * mm, "end": v(5.07, 19.03) * mm});
            skLineSegment(sketch, "E136", {"start": v(0.07, 19) * mm, "end": v(-4.93, 18.98) * mm});
            skPoint(sketch, "E137.endSnap0", {"position": v(-2.43, 19) * mm});
            skLineSegment(sketch, "E138", {"start": v(0, 10.95) * mm, "end": v(-4.93, 10.95) * mm});
            skLineSegment(sketch, "E139", {"start": v(0, 10.95) * mm, "end": v(5.07, 10.95) * mm});
            skLineSegment(sketch, "E140", {"start": v(1.78, 15) * mm, "end": v(1.81, 7) * mm});
            skLineSegment(sketch, "E141", {"start": v(-1.6, 23) * mm, "end": v(-1.6, 7) * mm});
            skLineSegment(sketch, "E142", {"start": v(-1.6, 19) * mm, "end": v(1.78, 15) * mm});
            skLineSegment(sketch, "E143", {"start": v(1.76, 19) * mm, "end": v(-1.6, 15) * mm});
            skLineSegment(sketch, "E144", {"start": v(-1.6, 15) * mm, "end": v(1.8, 11) * mm});
            skLineSegment(sketch, "E145", {"start": v(-1.6, 10.95) * mm, "end": v(1.78, 15) * mm});
            skSolve(sketch);
        }
        {
            var Q0;
            Q0=sQuery(id+"F15.wireOp",VERTEX,"E130.bottom.start");
            var Q1;
            Q1=sQuery(id+"F15.wireOp",VERTEX,"E141.start");
            var Q2;
            Q2=sQuery(id+"F15.wireOp",VERTEX,"E132.end");
            var Q3;
            Q3=sQuery(id+"F15.wireOp",VERTEX,"E130.bottom.end");
            var Q4;
            Q4=sQuery(id+"F15.wireOp",VERTEX,"E136.end");
            var Q5;
            Q5=sQuery(id+"F15.wireOp",VERTEX,"E143.start");
            var Q6;
            Q6=sQuery(id+"F15.wireOp",VERTEX,"E135.end");
            var Q7;
            Q7=sQuery(id+"F15.wireOp",VERTEX,"E142.start");
            var Q8;
            Q8=sQuery(id+"F15.wireOp",VERTEX,"E134.end");
            var Q9;
            Q9=sQuery(id+"F15.wireOp",VERTEX,"E143.end");
            var Q10;
            Q10=sQuery(id+"F15.wireOp",VERTEX,"E131.start");
            var Q11;
            Q11=sQuery(id+"F15.wireOp",VERTEX,"E133.end");
            var Q12;
            Q12=sQuery(id+"F15.wireOp",VERTEX,"E138.end");
            var Q13;
            Q13=sQuery(id+"F15.wireOp",VERTEX,"E145.start");
            var Q14;
            Q14=sQuery(id+"F15.wireOp",VERTEX,"E144.end");
            var Q15;
            Q15=sQuery(id+"F15.wireOp",VERTEX,"E139.end");
            var Q16;
            Q16=sQuery(id+"F15.wireOp",VERTEX,"E130.top.start");
            var Q17;
            Q17=sQuery(id+"F15.wireOp",VERTEX,"E141.end");
            var Q18;
            Q18=sQuery(id+"F15.wireOp",VERTEX,"E140.end");
            var Q19;
            Q19=sQuery(id+"F15.wireOp",VERTEX,"E130.top.end");
            var Q20;
            Q20=makeQuery(id+"F1.opExtrude","SWEPT_BODY",BODY,{"disambiguationData":[OSD([sQuery(id+"F0.wireOp",EDGE,"E0"),sQuery(id+"F0.wireOp",EDGE,"E1"),sQuery(id+"F0.wireOp",EDGE,"E2"),sQuery(id+"F0.wireOp",EDGE,"E3"),sQuery(id+"F0.wireOp",EDGE,"E4"),sQuery(id+"F0.wireOp",EDGE,"E5"),sQuery(id+"F0.wireOp",EDGE,"E6"),sQuery(id+"F0.wireOp",EDGE,"E7")])]});
            hole(context, id + "F16", {"style" : HoleStyle.SIMPLE, "endStyle" : HoleEndStyle.BLIND, "holeDiameter" : 2.5 * mm, "majorDiameter" : 5 * mm, "holeDepth" : 4 * mm, "isTappedThrough" : true, "tappedDepth" : 12 * mm, "tapClearance" : 3, "startFromSketch" : true, "locations" : qUnion([Q0, Q1, Q2, Q3, Q4, Q5, Q6, Q7, Q8, Q9, Q10, Q11, Q12, Q13, Q14, Q15, Q16, Q17, Q18, Q19]), "scope" : qUnion([Q20])});
        }
        {
            var Q0;
            Q0=makeQuery(id+"F2.imprint","IMPRINT",FACE,{"disambiguationData":[TD([[makeQuery(id+"F2.imprint","IMPRINT",EDGE,{"derivedFrom":sQuery(id+"F2.wireOp",EDGE,"E8")}),-1.0]])]});
            extrude(context, id + "F17", {"entities" : qUnion([Q0]), "operationType" : NewBodyOperationType.REMOVE, "oppositeDirection" : true, "depth" : 0.5 * mm, "offsetDistance" : 25 * mm});
        }
        {
            var Q0;
            Q0=makeQuery(id+"F4.boolean.opBoolean","COPY",FACE,{"derivedFrom":makeQuery(id+"F4.opExtrude","CAP_FACE",FACE,{"disambiguationData":[OSD([sQuery(id+"F3.wireOp",EDGE,"E16"),sQuery(id+"F3.wireOp",EDGE,"E17"),sQuery(id+"F3.wireOp",EDGE,"E18"),sQuery(id+"F3.wireOp",EDGE,"E19"),sQuery(id+"F3.wireOp",EDGE,"E20"),sQuery(id+"F3.wireOp",EDGE,"E21"),sQuery(id+"F3.wireOp",EDGE,"E22"),sQuery(id+"F3.wireOp",EDGE,"E23")])],"isStart":false})});
            var sketch = newSketch(context, id + "F18", { "sketchPlane" : qUnion([Q0])});
            skLineSegment(sketch, "E146.bottom", {"start": v(16.54, 5.96) * mm, "end": v(36.54, 5.96) * mm});
            skLineSegment(sketch, "E146.top", {"start": v(15.98, 0) * mm, "end": v(36.54, 0) * mm});
            skLineSegment(sketch, "E146.right", {"start": v(36.54, 5.96) * mm, "end": v(36.54, 0) * mm});
            skLineSegment(sketch, "E147.bottom", {"start": v(36.54, 5.96) * mm, "end": v(33.54, 5.96) * mm});
            skLineSegment(sketch, "E147.top", {"start": v(36.54, 17.96) * mm, "end": v(33.54, 17.96) * mm});
            skLineSegment(sketch, "E147.left", {"start": v(36.54, 5.96) * mm, "end": v(36.54, 17.96) * mm});
            skLineSegment(sketch, "E147.right", {"start": v(33.54, 5.96) * mm, "end": v(33.54, 17.96) * mm});
            skLineSegment(sketch, "E148", {"start": v(36.54, 2.98) * mm, "end": v(15.95, 2.98) * mm});
            skLineSegment(sketch, "E149", {"start": v(36.54, 5.96) * mm, "end": v(36.54, 8.96) * mm});
            skLineSegment(sketch, "E150", {"start": v(36.54, 8.96) * mm, "end": v(18.93, 8.96) * mm});
            skLineSegment(sketch, "E151", {"start": v(36.54, 8.96) * mm, "end": v(36.54, 11.96) * mm});
            skLineSegment(sketch, "E152", {"start": v(36.54, 11.96) * mm, "end": v(22.15, 11.96) * mm});
            skLineSegment(sketch, "E153", {"start": v(36.54, 11.96) * mm, "end": v(36.54, 14.96) * mm});
            skLineSegment(sketch, "E154", {"start": v(36.54, 14.96) * mm, "end": v(25.54, 14.96) * mm});
            skLineSegment(sketch, "E155", {"start": v(33.54, 17.96) * mm, "end": v(28.85, 17.96) * mm});
            skLineSegment(sketch, "E156", {"start": v(33.54, 17.96) * mm, "end": v(33.54, 20.54) * mm});
            skLineSegment(sketch, "E157", {"start": v(33.54, 20.54) * mm, "end": v(31.81, 20.54) * mm});
            skLineSegment(sketch, "E158", {"start": v(33.54, 20.54) * mm, "end": v(36.54, 20.54) * mm});
            skLineSegment(sketch, "E159", {"start": v(33.54, 20.54) * mm, "end": v(33.54, 22.3) * mm});
            skLineSegment(sketch, "E160", {"start": v(16.54, 5.96) * mm, "end": v(33.54, 22.3) * mm});
            skPoint(sketch, "E161.orphan", {"position": v(33.54, 24.06) * mm});
            skLineSegment(sketch, "E162", {"start": v(33.54, 5.96) * mm, "end": v(33.54, 0) * mm});
            skLineSegment(sketch, "E163", {"start": v(33.54, 0) * mm, "end": v(30.54, 0) * mm});
            skLineSegment(sketch, "E164", {"start": v(30.54, 0) * mm, "end": v(30.54, 19.41) * mm});
            skLineSegment(sketch, "E165", {"start": v(30.54, 0) * mm, "end": v(27.54, 0) * mm});
            skLineSegment(sketch, "E166", {"start": v(27.54, 0) * mm, "end": v(27.54, 16.53) * mm});
            skLineSegment(sketch, "E167", {"start": v(27.54, 0) * mm, "end": v(24.54, 0) * mm});
            skLineSegment(sketch, "E168", {"start": v(24.54, 0) * mm, "end": v(21.54, 0) * mm});
            skLineSegment(sketch, "E169", {"start": v(18.93, 0) * mm, "end": v(18.93, 8.26) * mm});
            skLineSegment(sketch, "E170", {"start": v(21.54, 0) * mm, "end": v(21.54, 10.77) * mm});
            skLineSegment(sketch, "E171", {"start": v(24.54, 0) * mm, "end": v(24.54, 13.65) * mm});
            skLineSegment(sketch, "E172", {"start": v(36.54, 17.96) * mm, "end": v(36.54, 20.54) * mm});
            skPoint(sketch, "E173.orphan", {"position": v(16.54, -6) * mm});
            skPoint(sketch, "E174.end.orphan", {"position": v(16.26, -3) * mm});
            skPoint(sketch, "E174.start.orphan", {"position": v(36.54, -3) * mm});
            skPoint(sketch, "E175.top.end.orphan", {"position": v(36.54, -6) * mm});
            skLineSegment(sketch, "E176", {"start": v(18.93, 2.98) * mm, "end": v(21.54, 0) * mm});
            skLineSegment(sketch, "E177", {"start": v(21.54, 2.98) * mm, "end": v(24.54, 0) * mm});
            skLineSegment(sketch, "E178", {"start": v(24.57, 2.98) * mm, "end": v(27.54, 0) * mm});
            skLineSegment(sketch, "E179", {"start": v(27.54, 2.98) * mm, "end": v(30.54, 0) * mm});
            skLineSegment(sketch, "E180", {"start": v(30.54, 2.98) * mm, "end": v(33.54, 0) * mm});
            skLineSegment(sketch, "E181", {"start": v(33.54, 2.98) * mm, "end": v(36.54, 0) * mm});
            skLineSegment(sketch, "E182", {"start": v(18.93, 5.96) * mm, "end": v(21.54, 5.96) * mm});
            skLineSegment(sketch, "E183", {"start": v(21.54, 5.96) * mm, "end": v(24.57, 2.98) * mm});
            skLineSegment(sketch, "E184", {"start": v(24.57, 5.96) * mm, "end": v(27.54, 2.98) * mm});
            skLineSegment(sketch, "E185", {"start": v(27.54, 5.96) * mm, "end": v(30.54, 2.98) * mm});
            skLineSegment(sketch, "E186", {"start": v(30.54, 5.96) * mm, "end": v(33.54, 2.98) * mm});
            skLineSegment(sketch, "E187", {"start": v(33.57, 6.01) * mm, "end": v(36.54, 2.98) * mm});
            skLineSegment(sketch, "E188", {"start": v(21.54, 9) * mm, "end": v(24.57, 5.96) * mm});
            skLineSegment(sketch, "E189", {"start": v(24.55, 9.06) * mm, "end": v(27.54, 5.96) * mm});
            skLineSegment(sketch, "E190", {"start": v(27.56, 9.03) * mm, "end": v(30.54, 5.96) * mm});
            skLineSegment(sketch, "E191", {"start": v(30.54, 9) * mm, "end": v(33.57, 6.01) * mm});
            skLineSegment(sketch, "E192", {"start": v(33.62, 8.96) * mm, "end": v(36.54, 5.96) * mm});
            skLineSegment(sketch, "E193", {"start": v(24.54, 11.96) * mm, "end": v(27.56, 9.03) * mm});
            skLineSegment(sketch, "E194", {"start": v(27.54, 12) * mm, "end": v(30.54, 9) * mm});
            skLineSegment(sketch, "E195", {"start": v(30.64, 12) * mm, "end": v(33.62, 8.96) * mm});
            skLineSegment(sketch, "E196", {"start": v(33.55, 12.03) * mm, "end": v(36.54, 8.96) * mm});
            skLineSegment(sketch, "E197", {"start": v(27.54, 15.05) * mm, "end": v(30.64, 12) * mm});
            skLineSegment(sketch, "E198", {"start": v(30.57, 15.01) * mm, "end": v(33.55, 12.03) * mm});
            skLineSegment(sketch, "E199", {"start": v(33.55, 15.05) * mm, "end": v(36.54, 11.96) * mm});
            skLineSegment(sketch, "E200", {"start": v(30.54, 17.96) * mm, "end": v(33.55, 15.05) * mm});
            skLineSegment(sketch, "E201", {"start": v(33.54, 17.96) * mm, "end": v(36.54, 14.96) * mm});
            skLineSegment(sketch, "E202", {"start": v(33.54, 20.54) * mm, "end": v(36.54, 17.96) * mm});
            skLineSegment(sketch, "E203", {"start": v(18.93, 8.26) * mm, "end": v(18.93, 9) * mm});
            skLineSegment(sketch, "E204", {"start": v(22.15, 11.96) * mm, "end": v(21.54, 11.96) * mm});
            skLineSegment(sketch, "E205", {"start": v(21.54, 11.96) * mm, "end": v(21.54, 10.77) * mm});
            skLineSegment(sketch, "E206", {"start": v(24.54, 13.65) * mm, "end": v(24.54, 14.96) * mm});
            skLineSegment(sketch, "E207", {"start": v(24.54, 14.96) * mm, "end": v(25.54, 14.96) * mm});
            skLineSegment(sketch, "E208", {"start": v(27.54, 16.53) * mm, "end": v(27.54, 17.96) * mm});
            skLineSegment(sketch, "E209", {"start": v(27.54, 17.96) * mm, "end": v(28.85, 17.96) * mm});
            skLineSegment(sketch, "E210", {"start": v(30.54, 19.41) * mm, "end": v(30.54, 20.54) * mm});
            skLineSegment(sketch, "E211", {"start": v(30.54, 20.54) * mm, "end": v(31.81, 20.54) * mm});
            skLineSegment(sketch, "E212", {"start": v(30.54, 20.54) * mm, "end": v(33.54, 17.96) * mm});
            skLineSegment(sketch, "E213", {"start": v(27.54, 17.96) * mm, "end": v(30.57, 15.01) * mm});
            skLineSegment(sketch, "E214", {"start": v(24.54, 14.96) * mm, "end": v(27.54, 12) * mm});
            skLineSegment(sketch, "E215", {"start": v(21.54, 11.96) * mm, "end": v(24.55, 9.06) * mm});
            skLineSegment(sketch, "E216", {"start": v(18.93, 8.96) * mm, "end": v(21.54, 5.96) * mm});
            skLineSegment(sketch, "E217", {"start": v(15.98, 0) * mm, "end": v(15.98, 5.96) * mm});
            skLineSegment(sketch, "E218", {"start": v(15.98, 5.96) * mm, "end": v(16.54, 5.96) * mm});
            skLineSegment(sketch, "E219", {"start": v(15.95, 2.98) * mm, "end": v(18.93, 0) * mm});
            skLineSegment(sketch, "E220", {"start": v(15.98, 5.96) * mm, "end": v(18.93, 2.98) * mm});
            skLineSegment(sketch, "E221", {"start": v(18.93, 5.96) * mm, "end": v(21.54, 2.98) * mm});
            skLineSegment(sketch, "E222.MirrorCS", {"start": v(33.54, -20.54) * mm, "end": v(33.54, -22.3) * mm});
            skLineSegment(sketch, "E223.MirrorCS", {"start": v(30.54, -20.54) * mm, "end": v(31.81, -20.54) * mm});
            skLineSegment(sketch, "E224.MirrorCS", {"start": v(30.54, -19.41) * mm, "end": v(30.54, -20.54) * mm});
            skLineSegment(sketch, "E225.MirrorCS", {"start": v(27.54, -17.96) * mm, "end": v(28.85, -17.96) * mm});
            skLineSegment(sketch, "E226.MirrorCS", {"start": v(36.54, -5.96) * mm, "end": v(33.54, -5.96) * mm});
            skLineSegment(sketch, "E227.MirrorCS", {"start": v(33.54, -17.96) * mm, "end": v(33.54, -20.54) * mm});
            skLineSegment(sketch, "E228.MirrorCS", {"start": v(36.54, -11.96) * mm, "end": v(36.54, -14.96) * mm});
            skLineSegment(sketch, "E229.MirrorCS", {"start": v(36.54, -17.96) * mm, "end": v(36.54, -20.54) * mm});
            skLineSegment(sketch, "E230.MirrorCS", {"start": v(33.57, -6.01) * mm, "end": v(36.54, -2.98) * mm});
            skLineSegment(sketch, "E231.MirrorCS", {"start": v(27.54, -2.98) * mm, "end": v(30.54, 0) * mm});
            skLineSegment(sketch, "E232.MirrorCS", {"start": v(33.54, -17.96) * mm, "end": v(36.54, -14.96) * mm});
            skLineSegment(sketch, "E233.MirrorCS", {"start": v(33.54, -20.54) * mm, "end": v(31.81, -20.54) * mm});
            skLineSegment(sketch, "E234.MirrorCS", {"start": v(30.64, -12) * mm, "end": v(33.62, -8.96) * mm});
            skLineSegment(sketch, "E235.MirrorCS", {"start": v(36.54, -8.96) * mm, "end": v(36.54, -11.96) * mm});
            skLineSegment(sketch, "E236.MirrorCS", {"start": v(33.54, -20.54) * mm, "end": v(36.54, -20.54) * mm});
            skLineSegment(sketch, "E237.MirrorCS", {"start": v(27.56, -9.03) * mm, "end": v(30.54, -5.96) * mm});
            skLineSegment(sketch, "E238.MirrorCS", {"start": v(36.54, -2.98) * mm, "end": v(15.95, -2.98) * mm});
            skLineSegment(sketch, "E239.MirrorCS", {"start": v(30.54, -2.98) * mm, "end": v(33.54, 0) * mm});
            skLineSegment(sketch, "E240.MirrorCS", {"start": v(33.54, -5.96) * mm, "end": v(33.54, -17.96) * mm});
            skLineSegment(sketch, "E241.MirrorCS", {"start": v(16.54, -5.96) * mm, "end": v(36.54, -5.96) * mm});
            skLineSegment(sketch, "E242.MirrorCS", {"start": v(33.54, -2.98) * mm, "end": v(36.54, 0) * mm});
            skLineSegment(sketch, "E243.MirrorCS", {"start": v(27.54, -15.05) * mm, "end": v(30.64, -12) * mm});
            skLineSegment(sketch, "E244.MirrorCS", {"start": v(30.54, -9) * mm, "end": v(33.57, -6.01) * mm});
            skLineSegment(sketch, "E245.MirrorCS", {"start": v(27.54, -12) * mm, "end": v(30.54, -9) * mm});
            skLineSegment(sketch, "E246.MirrorCS", {"start": v(36.54, -8.96) * mm, "end": v(18.93, -8.96) * mm});
            skLineSegment(sketch, "E247.MirrorCS", {"start": v(36.54, -11.96) * mm, "end": v(22.15, -11.96) * mm});
            skLineSegment(sketch, "E248.MirrorCS", {"start": v(33.54, -20.54) * mm, "end": v(36.54, -17.96) * mm});
            skLineSegment(sketch, "E249.MirrorCS", {"start": v(36.54, -5.96) * mm, "end": v(36.54, 0) * mm});
            skLineSegment(sketch, "E250.MirrorCS", {"start": v(33.55, -12.03) * mm, "end": v(36.54, -8.96) * mm});
            skLineSegment(sketch, "E251.MirrorCS", {"start": v(27.54, -17.96) * mm, "end": v(30.57, -15.01) * mm});
            skLineSegment(sketch, "E252.MirrorCS", {"start": v(33.54, -17.96) * mm, "end": v(28.85, -17.96) * mm});
            skLineSegment(sketch, "E253.MirrorCS", {"start": v(27.54, -5.96) * mm, "end": v(30.54, -2.98) * mm});
            skLineSegment(sketch, "E254.MirrorCS", {"start": v(36.54, -5.96) * mm, "end": v(36.54, -8.96) * mm});
            skLineSegment(sketch, "E255.MirrorCS", {"start": v(30.57, -15.01) * mm, "end": v(33.55, -12.03) * mm});
            skLineSegment(sketch, "E256.MirrorCS", {"start": v(33.62, -8.96) * mm, "end": v(36.54, -5.96) * mm});
            skLineSegment(sketch, "E257.MirrorCS", {"start": v(33.55, -15.05) * mm, "end": v(36.54, -11.96) * mm});
            skLineSegment(sketch, "E258.MirrorCS", {"start": v(36.54, -5.96) * mm, "end": v(36.54, -17.96) * mm});
            skLineSegment(sketch, "E259.MirrorCS", {"start": v(30.54, -20.54) * mm, "end": v(33.54, -17.96) * mm});
            skLineSegment(sketch, "E260.MirrorCS", {"start": v(33.54, -5.96) * mm, "end": v(33.54, 0) * mm});
            skLineSegment(sketch, "E261.MirrorCS", {"start": v(36.54, -17.96) * mm, "end": v(33.54, -17.96) * mm});
            skLineSegment(sketch, "E262.MirrorCS", {"start": v(36.54, -14.96) * mm, "end": v(25.54, -14.96) * mm});
            skLineSegment(sketch, "E263.MirrorCS", {"start": v(30.54, -17.96) * mm, "end": v(33.55, -15.05) * mm});
            skLineSegment(sketch, "E264.MirrorCS", {"start": v(30.54, -5.96) * mm, "end": v(33.54, -2.98) * mm});
            skLineSegment(sketch, "E265.MirrorCS", {"start": v(16.54, -5.96) * mm, "end": v(33.54, -22.3) * mm});
            skLineSegment(sketch, "E266.MirrorCS", {"start": v(30.54, 0) * mm, "end": v(30.54, -19.41) * mm});
            skLineSegment(sketch, "E267.MirrorCS", {"start": v(24.54, -14.96) * mm, "end": v(25.54, -14.96) * mm});
            skLineSegment(sketch, "E268.MirrorCS", {"start": v(24.54, -13.65) * mm, "end": v(24.54, -14.96) * mm});
            skLineSegment(sketch, "E269.MirrorCS", {"start": v(21.54, -5.96) * mm, "end": v(24.57, -2.98) * mm});
            skLineSegment(sketch, "E270.MirrorCS", {"start": v(21.54, -9) * mm, "end": v(24.57, -5.96) * mm});
            skLineSegment(sketch, "E271.MirrorCS", {"start": v(24.54, -14.96) * mm, "end": v(27.54, -12) * mm});
            skLineSegment(sketch, "E272.MirrorCS", {"start": v(24.57, -5.96) * mm, "end": v(27.54, -2.98) * mm});
            skLineSegment(sketch, "E273.MirrorCS", {"start": v(24.55, -9.06) * mm, "end": v(27.54, -5.96) * mm});
            skLineSegment(sketch, "E274.MirrorCS", {"start": v(24.57, -2.98) * mm, "end": v(27.54, 0) * mm});
            skLineSegment(sketch, "E275.MirrorCS", {"start": v(21.54, -11.96) * mm, "end": v(24.55, -9.06) * mm});
            skLineSegment(sketch, "E276.MirrorCS", {"start": v(24.54, -11.96) * mm, "end": v(27.56, -9.03) * mm});
            skLineSegment(sketch, "E277.MirrorCS", {"start": v(24.54, 0) * mm, "end": v(24.54, -13.65) * mm});
            skLineSegment(sketch, "E278.MirrorCS", {"start": v(27.54, 0) * mm, "end": v(27.54, -16.53) * mm});
            skLineSegment(sketch, "E279.MirrorCS", {"start": v(15.98, -5.96) * mm, "end": v(16.54, -5.96) * mm});
            skLineSegment(sketch, "E280.MirrorCS", {"start": v(18.93, -8.26) * mm, "end": v(18.93, -9) * mm});
            skLineSegment(sketch, "E281.MirrorCS", {"start": v(18.93, -5.96) * mm, "end": v(21.54, -5.96) * mm});
            skLineSegment(sketch, "E282.MirrorCS", {"start": v(21.54, -2.98) * mm, "end": v(24.54, 0) * mm});
            skLineSegment(sketch, "E283.MirrorCS", {"start": v(21.54, 0) * mm, "end": v(21.54, -10.77) * mm});
            skLineSegment(sketch, "E284.MirrorCS", {"start": v(18.93, -8.96) * mm, "end": v(21.54, -5.96) * mm});
            skLineSegment(sketch, "E285.MirrorCS", {"start": v(18.93, -5.96) * mm, "end": v(21.54, -2.98) * mm});
            skLineSegment(sketch, "E286.MirrorCS", {"start": v(15.95, -2.98) * mm, "end": v(18.93, 0) * mm});
            skLineSegment(sketch, "E287.MirrorCS", {"start": v(18.93, 0) * mm, "end": v(18.93, -8.26) * mm});
            skLineSegment(sketch, "E288.MirrorCS", {"start": v(15.98, -5.96) * mm, "end": v(18.93, -2.98) * mm});
            skLineSegment(sketch, "E289.MirrorCS", {"start": v(15.98, 0) * mm, "end": v(15.98, -5.96) * mm});
            skLineSegment(sketch, "E290.MirrorCS", {"start": v(18.93, -2.98) * mm, "end": v(21.54, 0) * mm});
            skLineSegment(sketch, "E291", {"start": v(33.54, 20.54) * mm, "end": v(33.54, 23.54) * mm});
            skLineSegment(sketch, "E292", {"start": v(33.54, -20.54) * mm, "end": v(33.54, -23.54) * mm});
            skSolve(sketch);
        }
        {
            var Q0;
            Q0=sQuery(id+"F18.wireOp",VERTEX,"E210.end");
            var Q1;
            Q1=sQuery(id+"F18.wireOp",VERTEX,"E156.end");
            var Q2;
            Q2=sQuery(id+"F18.wireOp",VERTEX,"E158.end");
            var Q3;
            Q3=sQuery(id+"F18.wireOp",VERTEX,"E208.end");
            var Q4;
            Q4=sQuery(id+"F18.wireOp",VERTEX,"E200.start");
            var Q5;
            Q5=sQuery(id+"F18.wireOp",VERTEX,"E147.top.end");
            var Q6;
            Q6=sQuery(id+"F18.wireOp",VERTEX,"E147.top.start");
            var Q7;
            Q7=sQuery(id+"F18.wireOp",VERTEX,"E206.end");
            var Q8;
            Q8=sQuery(id+"F18.wireOp",VERTEX,"E197.start");
            var Q9;
            Q9=sQuery(id+"F18.wireOp",VERTEX,"E198.start");
            var Q10;
            Q10=sQuery(id+"F18.wireOp",VERTEX,"E199.start");
            var Q11;
            Q11=sQuery(id+"F18.wireOp",VERTEX,"E153.end");
            var Q12;
            Q12=sQuery(id+"F18.wireOp",VERTEX,"E204.end");
            var Q13;
            Q13=sQuery(id+"F18.wireOp",VERTEX,"E193.start");
            var Q14;
            Q14=sQuery(id+"F18.wireOp",VERTEX,"E194.start");
            var Q15;
            Q15=sQuery(id+"F18.wireOp",VERTEX,"E195.start");
            var Q16;
            Q16=sQuery(id+"F18.wireOp",VERTEX,"E196.start");
            var Q17;
            Q17=sQuery(id+"F18.wireOp",VERTEX,"E151.end");
            var Q18;
            Q18=sQuery(id+"F18.wireOp",VERTEX,"E150.end");
            var Q19;
            Q19=sQuery(id+"F18.wireOp",VERTEX,"E188.start");
            var Q20;
            Q20=sQuery(id+"F18.wireOp",VERTEX,"E189.start");
            var Q21;
            Q21=sQuery(id+"F18.wireOp",VERTEX,"E190.start");
            var Q22;
            Q22=sQuery(id+"F18.wireOp",VERTEX,"E191.start");
            var Q23;
            Q23=sQuery(id+"F18.wireOp",VERTEX,"E192.start");
            var Q24;
            Q24=sQuery(id+"F18.wireOp",VERTEX,"E149.end");
            var Q25;
            Q25=sQuery(id+"F18.wireOp",VERTEX,"E217.end");
            var Q26;
            Q26=sQuery(id+"F18.wireOp",VERTEX,"E182.start");
            var Q27;
            Q27=sQuery(id+"F18.wireOp",VERTEX,"E182.end");
            var Q28;
            Q28=sQuery(id+"F18.wireOp",VERTEX,"E184.start");
            var Q29;
            Q29=sQuery(id+"F18.wireOp",VERTEX,"E185.start");
            var Q30;
            Q30=sQuery(id+"F18.wireOp",VERTEX,"E186.start");
            var Q31;
            Q31=sQuery(id+"F18.wireOp",VERTEX,"E147.bottom.end");
            var Q32;
            Q32=sQuery(id+"F18.wireOp",VERTEX,"E146.bottom.end");
            var Q33;
            Q33=sQuery(id+"F18.wireOp",VERTEX,"E148.end");
            var Q34;
            Q34=sQuery(id+"F18.wireOp",VERTEX,"E177.start");
            var Q35;
            Q35=sQuery(id+"F18.wireOp",VERTEX,"E176.start");
            var Q36;
            Q36=sQuery(id+"F18.wireOp",VERTEX,"E178.start");
            var Q37;
            Q37=sQuery(id+"F18.wireOp",VERTEX,"E179.start");
            var Q38;
            Q38=sQuery(id+"F18.wireOp",VERTEX,"E180.start");
            var Q39;
            Q39=sQuery(id+"F18.wireOp",VERTEX,"E181.start");
            var Q40;
            Q40=sQuery(id+"F18.wireOp",VERTEX,"E148.start");
            var Q41;
            Q41=sQuery(id+"F18.wireOp",VERTEX,"E146.top.start");
            var Q42;
            Q42=sQuery(id+"F18.wireOp",VERTEX,"E169.start");
            var Q43;
            Q43=sQuery(id+"F18.wireOp",VERTEX,"E168.end");
            var Q44;
            Q44=sQuery(id+"F18.wireOp",VERTEX,"E167.end");
            var Q45;
            Q45=sQuery(id+"F18.wireOp",VERTEX,"E165.end");
            var Q46;
            Q46=sQuery(id+"F18.wireOp",VERTEX,"E163.end");
            var Q47;
            Q47=sQuery(id+"F18.wireOp",VERTEX,"E162.end");
            var Q48;
            Q48=sQuery(id+"F18.wireOp",VERTEX,"E146.top.end");
            var Q49;
            Q49=sQuery(id+"F18.wireOp",VERTEX,"E288.MirrorCS.end");
            var Q50;
            Q50=sQuery(id+"F18.wireOp",VERTEX,"E238.MirrorCS.end");
            var Q51;
            Q51=sQuery(id+"F18.wireOp",VERTEX,"E282.MirrorCS.start");
            var Q52;
            Q52=sQuery(id+"F18.wireOp",VERTEX,"E269.MirrorCS.end");
            var Q53;
            Q53=sQuery(id+"F18.wireOp",VERTEX,"E231.MirrorCS.start");
            var Q54;
            Q54=sQuery(id+"F18.wireOp",VERTEX,"E239.MirrorCS.start");
            var Q55;
            Q55=sQuery(id+"F18.wireOp",VERTEX,"E242.MirrorCS.start");
            var Q56;
            Q56=sQuery(id+"F18.wireOp",VERTEX,"E279.MirrorCS.start");
            var Q57;
            Q57=sQuery(id+"F18.wireOp",VERTEX,"E281.MirrorCS.start");
            var Q58;
            Q58=sQuery(id+"F18.wireOp",VERTEX,"E174.start.orphan");
            var Q59;
            Q59=sQuery(id+"F18.wireOp",VERTEX,"E269.MirrorCS.start");
            var Q60;
            Q60=sQuery(id+"F18.wireOp",VERTEX,"E270.MirrorCS.end");
            var Q61;
            Q61=sQuery(id+"F18.wireOp",VERTEX,"E253.MirrorCS.start");
            var Q62;
            Q62=sQuery(id+"F18.wireOp",VERTEX,"E237.MirrorCS.end");
            var Q63;
            Q63=sQuery(id+"F18.wireOp",VERTEX,"E226.MirrorCS.end");
            var Q64;
            Q64=sQuery(id+"F18.wireOp",VERTEX,"E175.top.end.orphan");
            var Q65;
            Q65=sQuery(id+"F18.wireOp",VERTEX,"E246.MirrorCS.end");
            var Q66;
            Q66=sQuery(id+"F18.wireOp",VERTEX,"E270.MirrorCS.start");
            var Q67;
            Q67=sQuery(id+"F18.wireOp",VERTEX,"E273.MirrorCS.start");
            var Q68;
            Q68=sQuery(id+"F18.wireOp",VERTEX,"E237.MirrorCS.start");
            var Q69;
            Q69=sQuery(id+"F18.wireOp",VERTEX,"E234.MirrorCS.end");
            var Q70;
            Q70=sQuery(id+"F18.wireOp",VERTEX,"E244.MirrorCS.start");
            var Q71;
            Q71=sQuery(id+"F18.wireOp",VERTEX,"E235.MirrorCS.start");
            var Q72;
            Q72=sQuery(id+"F18.wireOp",VERTEX,"E275.MirrorCS.start");
            var Q73;
            Q73=sQuery(id+"F18.wireOp",VERTEX,"E276.MirrorCS.start");
            var Q74;
            Q74=sQuery(id+"F18.wireOp",VERTEX,"E245.MirrorCS.start");
            var Q75;
            Q75=sQuery(id+"F18.wireOp",VERTEX,"E234.MirrorCS.start");
            var Q76;
            Q76=sQuery(id+"F18.wireOp",VERTEX,"E250.MirrorCS.start");
            var Q77;
            Q77=sQuery(id+"F18.wireOp",VERTEX,"E228.MirrorCS.start");
            var Q78;
            Q78=sQuery(id+"F18.wireOp",VERTEX,"E267.MirrorCS.start");
            var Q79;
            Q79=sQuery(id+"F18.wireOp",VERTEX,"E243.MirrorCS.start");
            var Q80;
            Q80=sQuery(id+"F18.wireOp",VERTEX,"E251.MirrorCS.end");
            var Q81;
            Q81=sQuery(id+"F18.wireOp",VERTEX,"E257.MirrorCS.start");
            var Q82;
            Q82=sQuery(id+"F18.wireOp",VERTEX,"E228.MirrorCS.end");
            var Q83;
            Q83=sQuery(id+"F18.wireOp",VERTEX,"E225.MirrorCS.start");
            var Q84;
            Q84=sQuery(id+"F18.wireOp",VERTEX,"E263.MirrorCS.start");
            var Q85;
            Q85=sQuery(id+"F18.wireOp",VERTEX,"E227.MirrorCS.start");
            var Q86;
            Q86=sQuery(id+"F18.wireOp",VERTEX,"E229.MirrorCS.start");
            var Q87;
            Q87=sQuery(id+"F18.wireOp",VERTEX,"E223.MirrorCS.start");
            var Q88;
            Q88=sQuery(id+"F18.wireOp",VERTEX,"E222.MirrorCS.start");
            var Q89;
            Q89=sQuery(id+"F18.wireOp",VERTEX,"E229.MirrorCS.end");
            var Q90;
            Q90=makeQuery(id+"F1.opExtrude","SWEPT_BODY",BODY,{"disambiguationData":[OSD([sQuery(id+"F0.wireOp",EDGE,"E0"),sQuery(id+"F0.wireOp",EDGE,"E1"),sQuery(id+"F0.wireOp",EDGE,"E2"),sQuery(id+"F0.wireOp",EDGE,"E3"),sQuery(id+"F0.wireOp",EDGE,"E4"),sQuery(id+"F0.wireOp",EDGE,"E5"),sQuery(id+"F0.wireOp",EDGE,"E6"),sQuery(id+"F0.wireOp",EDGE,"E7")])]});
            hole(context, id + "F19", {"style" : HoleStyle.SIMPLE, "endStyle" : HoleEndStyle.BLIND, "holeDiameter" : 2 * mm, "majorDiameter" : 5 * mm, "holeDepth" : 8 * mm, "isTappedThrough" : true, "tappedDepth" : 12 * mm, "tapClearance" : 3, "startFromSketch" : true, "locations" : qUnion([Q0, Q1, Q2, Q3, Q4, Q5, Q6, Q7, Q8, Q9, Q10, Q11, Q12, Q13, Q14, Q15, Q16, Q17, Q18, Q19, Q20, Q21, Q22, Q23, Q24, Q25, Q26, Q27, Q28, Q29, Q30, Q31, Q32, Q33, Q34, Q35, Q36, Q37, Q38, Q39, Q40, Q41, Q42, Q43, Q44, Q45, Q46, Q47, Q48, Q49, Q50, Q51, Q52, Q53, Q54, Q55, Q56, Q57, Q58, Q59, Q60, Q61, Q62, Q63, Q64, Q65, Q66, Q67, Q68, Q69, Q70, Q71, Q72, Q73, Q74, Q75, Q76, Q77, Q78, Q79, Q80, Q81, Q82, Q83, Q84, Q85, Q86, Q87, Q88, Q89]), "scope" : qUnion([Q90])});
        }
    });
